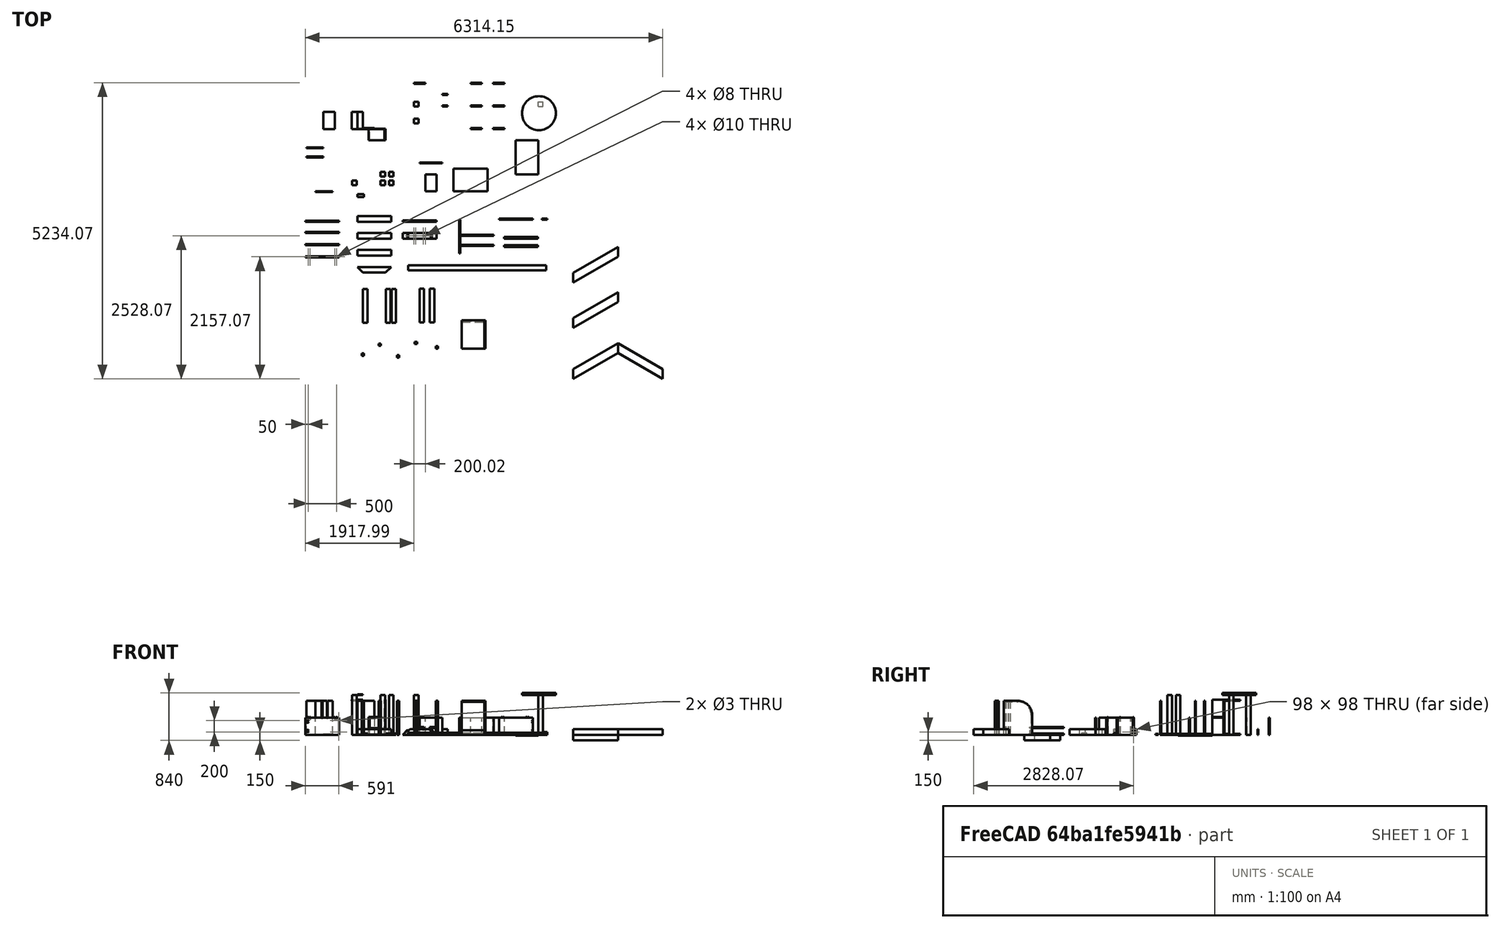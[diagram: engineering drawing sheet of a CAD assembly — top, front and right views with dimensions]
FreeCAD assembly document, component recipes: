
FREECAD ASSEMBLY — COMPONENT RECIPES ("Test001_features")

This assembly document has 28 components, labeled P0..P27 below (a component is one placed body or linked part). 21 of them carry a construction recipe — the FreeCAD feature program that regenerates the part from scratch, quoted from this document or its linked companion documents; the rest are supplied as boundary geometry only. No exploded tour is included for this assembly.
COMPONENT P0 — recipe-attached ("PDMirror Pad Body", modeled in this document).
Construction recipe (the document's own serialized feature program — sketch geometry with constraints, then the solid features built on it; lengths are millimeters unless a unit is written):

FEATURE [Sketcher::SketchObject] Sketch  label="Sketch001"
  ArcFitTolerance = 0
  AttachmentOffset = pos=(1300,-500,0) rot=(0,0,1;0rad)
  AttachmentSupport = -> [XY_Plane]
  ExternalTypes = [0]
  FullyConstrained = false
  MakeInternals = false
  MapMode = 5
  Placement = pos=(1300,-500,0) rot=(0,0,1;0rad)
  _ExternalGeoVersion = 0
  sketch-geometry (4):
    g0: LineSegment StartX=0 StartY=-90.3636 StartZ=0 EndX=200 EndY=-90.3636 EndZ=0
    g1: LineSegment StartX=200 StartY=-90.3636 StartZ=0 EndX=200 EndY=-108.364 EndZ=0
    g2: LineSegment StartX=200 StartY=-108.364 StartZ=0 EndX=0 EndY=-108.364 EndZ=0
    g3: LineSegment StartX=0 StartY=-108.364 StartZ=0 EndX=0 EndY=-90.3636 EndZ=0
  constraints (11):
    c: Coincident(g0,g1)
    c: Coincident(g1,g2)
    c: Coincident(g2,g3)
    c: Coincident(g3,g0)
    c: Horizontal(g0)
    c: Horizontal(g2)
    c: Vertical(g1)
    c: Vertical(g3)
    c: DistanceX(g0,g0) = 200
    c: DistanceY(g3,g3) = 18
    c: DistanceX(g-1,g0) = 200
FEATURE [PartDesign::Pad] Pad  label="PDMirror Pad"
  AllowMultiFace = false
  Direction = (0,0,1)
  Length = 300
  Length2 = 100
  Profile = -> Sketch
  SideType = 0
  Suppressed = false
  Type = 0
  Type2 = 0
FEATURE [PartDesign::Mirrored] Mirrored
  BaseFeature = -> Pad
  MirrorPlane = -> Sketch [V_Axis]
  Originals = -> [Pad]
  Suppressed = false
  TransformMode = 0
FEATURE [PartDesign::Body] Body  label="PDMirror Pad Body"
  AllowCompound = false
  Group = -> [Sketch,Pad,Mirrored]
  Origin = -> Origin
  Tip = -> Mirrored
COMPONENT P1 — recipe-attached ("Pad Single Body", modeled in this document).
Construction recipe (the document's own serialized feature program — sketch geometry with constraints, then the solid features built on it; lengths are millimeters unless a unit is written):

FEATURE [Sketcher::SketchObject] Sketch001  label="Sketch002"
  ArcFitTolerance = 0
  AttachmentOffset = pos=(1500,-1200,0) rot=(0,0,1;0rad)
  AttachmentSupport = -> [XY_Plane001]
  ExternalTypes = [0]
  FullyConstrained = true
  MakeInternals = false
  MapMode = 5
  Placement = pos=(1500,-1200,0) rot=(0,0,1;0rad)
  _ExternalGeoVersion = 0
  sketch-geometry (4):
    g0: LineSegment StartX=-300 StartY=400 StartZ=0 EndX=-100 EndY=400 EndZ=0
    g1: LineSegment StartX=-100 StartY=400 StartZ=0 EndX=-100 EndY=100 EndZ=0
    g2: LineSegment StartX=-100 StartY=100 StartZ=0 EndX=-300 EndY=100 EndZ=0
    g3: LineSegment StartX=-300 StartY=100 StartZ=0 EndX=-300 EndY=400 EndZ=0
  constraints (12):
    c: Coincident(g0,g1)
    c: Coincident(g1,g2)
    c: Coincident(g2,g3)
    c: Coincident(g3,g0)
    c: Horizontal(g0)
    c: Horizontal(g2)
    c: Vertical(g1)
    c: Vertical(g3)
    c: DistanceX(g0,g0) = 200
    c: DistanceY(g3,g3) = 300
    c: DistanceY(g-1,g0) = 400
    c: DistanceX(g1,g-1) = 100
FEATURE [PartDesign::Pad] Pad001  label="Pad Single"
  AllowMultiFace = false
  Direction = (0,0,1)
  Length = 18
  Length2 = 100
  Profile = -> Sketch001
  SideType = 0
  Suppressed = false
  Type = 0
  Type2 = 0
FEATURE [PartDesign::Body] Body001  label="Pad Single Body"
  AllowCompound = false
  Group = -> [Sketch001,Pad001]
  Origin = -> Origin001
  Tip = -> Pad001
COMPONENT P2 — recipe-attached ("PDMulti 4 Pad Body", modeled in this document).
Construction recipe (the document's own serialized feature program — sketch geometry with constraints, then the solid features built on it; lengths are millimeters unless a unit is written):

FEATURE [Sketcher::SketchObject] Sketch002  label="Sketch003"
  ArcFitTolerance = 0
  AttachmentOffset = pos=(2000,-900,0) rot=(0,0,1;0rad)
  AttachmentSupport = -> [XY_Plane002]
  ExternalTypes = [0]
  FullyConstrained = true
  MakeInternals = false
  MapMode = 5
  Placement = pos=(2000,-900,0) rot=(0,0,1;0rad)
  _ExternalGeoVersion = 0
  sketch-geometry (4):
    g0: LineSegment StartX=-300 StartY=200 StartZ=0 EndX=0 EndY=200 EndZ=0
    g1: LineSegment StartX=0 StartY=200 StartZ=0 EndX=0 EndY=0 EndZ=0
    g2: LineSegment StartX=0 StartY=0 StartZ=0 EndX=-300 EndY=0 EndZ=0
    g3: LineSegment StartX=-300 StartY=0 StartZ=0 EndX=-300 EndY=200 EndZ=0
  constraints (12):
    c: Coincident(g0,g1)
    c: Coincident(g1,g2)
    c: Coincident(g2,g3)
    c: Coincident(g3,g0)
    c: Horizontal(g0)
    c: Horizontal(g2)
    c: Vertical(g1)
    c: Vertical(g3)
    c: DistanceX(g0,g0) = 300
    c: DistanceY(g3,g3) = 200
    c: DistanceY(g1,g-1) = 0
    c: DistanceX(g1,g-1) = 0
FEATURE [PartDesign::Pad] Pad002  label="PDMulti 4 Pad"
  AllowMultiFace = false
  Direction = (0,0,1)
  Length = 18
  Length2 = 100
  Profile = -> Sketch002
  SideType = 0
  Suppressed = false
  Type = 0
  Type2 = 0
FEATURE [PartDesign::Mirrored] Mirrored001
  MirrorPlane = -> Sketch002 [V_Axis]
  Suppressed = false
  TransformMode = 0
FEATURE [PartDesign::Mirrored] Mirrored002
  MirrorPlane = -> Sketch002 [H_Axis]
  Suppressed = false
  TransformMode = 0
FEATURE [PartDesign::MultiTransform] MultiTransform
  BaseFeature = -> Pad002
  Originals = -> [Pad002]
  Suppressed = false
  TransformMode = 0
  Transformations = -> [Mirrored001,Mirrored002]
FEATURE [PartDesign::Body] Body002  label="PDMulti 4 Pad Body"
  AllowCompound = false
  Group = -> [Sketch002,Pad002,MultiTransform,Mirrored001,Mirrored002]
  Origin = -> Origin002
  Tip = -> MultiTransform
COMPONENT P3 — recipe-attached ("PDMulti 8 Pad Body", modeled in this document).
Construction recipe (the document's own serialized feature program — sketch geometry with constraints, then the solid features built on it; lengths are millimeters unless a unit is written):

FEATURE [Sketcher::SketchObject] Sketch003  label="Sketch004"
  ArcFitTolerance = 0
  AttachmentOffset = pos=(3000,-500,0) rot=(0,0,1;0rad)
  AttachmentSupport = -> [XY_Plane003]
  ExternalTypes = [0]
  FullyConstrained = true
  MakeInternals = false
  MapMode = 5
  Placement = pos=(3000,-500,0) rot=(0,0,1;0rad)
  _ExternalGeoVersion = 0
  sketch-geometry (4):
    g0: LineSegment StartX=-200 StartY=300 StartZ=0 EndX=0 EndY=300 EndZ=0
    g1: LineSegment StartX=0 StartY=300 StartZ=0 EndX=0 EndY=0 EndZ=0
    g2: LineSegment StartX=0 StartY=0 StartZ=0 EndX=-200 EndY=0 EndZ=0
    g3: LineSegment StartX=-200 StartY=0 StartZ=0 EndX=-200 EndY=300 EndZ=0
  constraints (11):
    c: Coincident(g0,g1)
    c: Coincident(g1,g2)
    c: Coincident(g2,g3)
    c: Coincident(g3,g0)
    c: Horizontal(g0)
    c: Horizontal(g2)
    c: Vertical(g1)
    c: Vertical(g3)
    c: Coincident(g1,g-1)
    c: DistanceX(g0,g0) = 200
    c: DistanceY(g3,g3) = 300
FEATURE [PartDesign::Pad] Pad003  label="PDMulti 8 Pad"
  AllowMultiFace = false
  Direction = (0,0,1)
  Length = 18
  Length2 = 100
  Profile = -> Sketch003
  SideType = 0
  Suppressed = false
  Type = 0
  Type2 = 0
FEATURE [PartDesign::Mirrored] Mirrored003
  MirrorPlane = -> Sketch003 [V_Axis]
  Suppressed = false
  TransformMode = 0
FEATURE [PartDesign::Mirrored] Mirrored004
  MirrorPlane = -> Sketch003 [H_Axis]
  Suppressed = false
  TransformMode = 0
FEATURE [PartDesign::Mirrored] Mirrored005
  MirrorPlane = -> XY_Plane003
  Suppressed = false
  TransformMode = 0
FEATURE [PartDesign::MultiTransform] MultiTransform001
  BaseFeature = -> Pad003
  Originals = -> [Pad003]
  Suppressed = false
  TransformMode = 0
  Transformations = -> [Mirrored003,Mirrored004,Mirrored005]
FEATURE [PartDesign::Body] Body003  label="PDMulti 8 Pad Body"
  AllowCompound = false
  Group = -> [Sketch003,Pad003,MultiTransform001,Mirrored003,Mirrored004,Mirrored005]
  Origin = -> Origin003
  Tip = -> MultiTransform001
COMPONENT P4 — recipe-attached ("Array Pad Body", modeled in this document).
Construction recipe (the document's own serialized feature program — sketch geometry with constraints, then the solid features built on it; lengths are millimeters unless a unit is written):

FEATURE [Sketcher::SketchObject] Sketch004  label="Sketch005"
  ArcFitTolerance = 0
  AttachmentOffset = pos=(500,-1000,0) rot=(0,0,1;0rad)
  AttachmentSupport = -> [XY_Plane004]
  ExternalTypes = [0]
  FullyConstrained = true
  MakeInternals = false
  MapMode = 5
  Placement = pos=(500,-1000,0) rot=(0,0,1;0rad)
  _ExternalGeoVersion = 0
  sketch-geometry (4):
    g0: LineSegment StartX=-90 StartY=90 StartZ=0 EndX=-10 EndY=90 EndZ=0
    g1: LineSegment StartX=-10 StartY=90 StartZ=0 EndX=-10 EndY=10 EndZ=0
    g2: LineSegment StartX=-10 StartY=10 StartZ=0 EndX=-90 EndY=10 EndZ=0
    g3: LineSegment StartX=-90 StartY=10 StartZ=0 EndX=-90 EndY=90 EndZ=0
  constraints (12):
    c: Coincident(g0,g1)
    c: Coincident(g1,g2)
    c: Coincident(g2,g3)
    c: Coincident(g3,g0)
    c: Horizontal(g0)
    c: Horizontal(g2)
    c: Vertical(g1)
    c: Vertical(g3)
    c: DistanceY(g-1,g1) = 10
    c: DistanceX(g1,g-1) = 10
    c: DistanceX(g0,g0) = 80
    c: DistanceY(g3,g3) = 80
FEATURE [PartDesign::Pad] Pad004  label="Array Pad"
  AllowMultiFace = false
  Direction = (0,0,1)
  Length = 700
  Length2 = 100
  Profile = -> Sketch004
  SideType = 0
  Suppressed = false
  Type = 0
  Type2 = 0
FEATURE [PartDesign::Body] Body004  label="Array Pad Body"
  AllowCompound = false
  Group = -> [Sketch004,Pad004]
  Origin = -> Origin004
  Tip = -> Pad004
COMPONENT P5 — recipe-attached ("Array Polar Pad Body", modeled in this document).
Construction recipe (the document's own serialized feature program — sketch geometry with constraints, then the solid features built on it; lengths are millimeters unless a unit is written):

FEATURE [Sketcher::SketchObject] Sketch005  label="Sketch006"
  ArcFitTolerance = 0
  AttachmentOffset = pos=(0,-1000,0) rot=(0,0,1;0rad)
  AttachmentSupport = -> [XY_Plane005]
  ExternalTypes = [0]
  FullyConstrained = true
  MakeInternals = false
  MapMode = 5
  Placement = pos=(0,-1000,0) rot=(0,0,1;0rad)
  _ExternalGeoVersion = 0
  sketch-geometry (4):
    g0: LineSegment StartX=-90 StartY=90 StartZ=0 EndX=-10 EndY=90 EndZ=0
    g1: LineSegment StartX=-10 StartY=90 StartZ=0 EndX=-10 EndY=10 EndZ=0
    g2: LineSegment StartX=-10 StartY=10 StartZ=0 EndX=-90 EndY=10 EndZ=0
    g3: LineSegment StartX=-90 StartY=10 StartZ=0 EndX=-90 EndY=90 EndZ=0
  constraints (12):
    c: Coincident(g0,g1)
    c: Coincident(g1,g2)
    c: Coincident(g2,g3)
    c: Coincident(g3,g0)
    c: Horizontal(g0)
    c: Horizontal(g2)
    c: Vertical(g1)
    c: Vertical(g3)
    c: DistanceY(g-1,g1) = 10
    c: DistanceX(g1,g-1) = 10
    c: DistanceX(g0,g0) = 80
    c: DistanceY(g3,g3) = 80
FEATURE [PartDesign::Pad] Pad005  label="Array Polar Pad"
  AllowMultiFace = false
  Direction = (0,0,1)
  Length = 700
  Length2 = 100
  Profile = -> Sketch005
  SideType = 0
  Suppressed = false
  Type = 0
  Type2 = 0
FEATURE [PartDesign::Body] Body005  label="Array Polar Pad Body"
  AllowCompound = false
  Group = -> [Sketch005,Pad005]
  Origin = -> Origin005
  Tip = -> Pad005
COMPONENT P6 — recipe-attached ("Table Top Parent Body", modeled in this document).
Construction recipe (the document's own serialized feature program — sketch geometry with constraints, then the solid features built on it; lengths are millimeters unless a unit is written):

FEATURE [Sketcher::SketchObject] Sketch006  label="Sketch007"
  ArcFitTolerance = 0
  AttachmentOffset = pos=(0,0,700) rot=(0,0,1;0rad)
  AttachmentSupport = -> [XY_Plane006]
  ExternalTypes = [0]
  FullyConstrained = false
  MakeInternals = false
  MapMode = 5
  Placement = pos=(0,0,700) rot=(0,0,1;0rad)
  _ExternalGeoVersion = 0
  sketch-geometry (1):
    g0: Circle CenterX=3208.45 CenterY=279.77 CenterZ=0 NormalX=0 NormalY=0 NormalZ=1 AngleXU=0 Radius=300
  constraints (1):
    c: Radius(g0) = 300  'This is my round table top radius'
FEATURE [PartDesign::Pad] Pad006  label="Table Top"
  Direction = (0,0,1)
  Length = 40
  Length2 = 100
  Profile = -> Sketch006
  SideType = 0
  Suppressed = false
  Type = 0
  Type2 = 0
FEATURE [PartDesign::Body] Body006  label="Table Top Parent Body"
  AllowCompound = false
  Group = -> [Sketch006,Pad006]
  Origin = -> Origin006
  Tip = -> Pad006
COMPONENT P7 — recipe-attached ("Screw, Body", modeled in this document).
Construction recipe (the document's own serialized feature program — sketch geometry with constraints, then the solid features built on it; lengths are millimeters unless a unit is written):

FEATURE [Sketcher::SketchObject] Sketch007  label="Core, Pattern"
  ArcFitTolerance = 0
  AttachmentSupport = -> [XZ_Plane007]
  ExternalTypes = [0]
  FullyConstrained = true
  MakeInternals = false
  MapMode = 5
  Placement = pos=(0,0,0) rot=(1,0,0;1.5708rad)
  _ExternalGeoVersion = 0
  expr: Constraints[10] = Spreadsheet.corer
  expr: Constraints[11] = 2 * Spreadsheet.tjump
  expr: Constraints[12] = Spreadsheet.sheight
  expr: Constraints[13] = Spreadsheet.hheight1
  expr: Constraints[14] = Spreadsheet.hheight2
  expr: Constraints[15] = Spreadsheet.hr
  expr: Constraints[16] = Spreadsheet.hheight1
  sketch-geometry (6):
    g0: LineSegment StartX=0 StartY=0 StartZ=0 EndX=1.5 EndY=3.8 EndZ=0
    g1: LineSegment StartX=1.5 StartY=3.8 StartZ=0 EndX=1.5 EndY=37 EndZ=0
    g2: LineSegment StartX=1.5 StartY=37 StartZ=0 EndX=2 EndY=37.5 EndZ=0
    g3: LineSegment StartX=2 StartY=37.5 StartZ=0 EndX=3.87 EndY=40 EndZ=0
    g4: LineSegment StartX=3.87 StartY=40 StartZ=0 EndX=0 EndY=40 EndZ=0
    g5: LineSegment StartX=0 StartY=40 StartZ=0 EndX=0 EndY=0 EndZ=0
  constraints (17):
    c: Coincident(g-1,g0)
    c: Coincident(g0,g1)
    c: Vertical(g1)
    c: Coincident(g1,g2)
    c: Coincident(g2,g3)
    c: Coincident(g3,g4)
    c: PointOnObject(g4,g-2)
    c: Horizontal(g4)
    c: Coincident(g4,g5)
    c: Coincident(g5,g0)
    c: DistanceX(g0,g0) = 1.5
    c: DistanceY(g0,g0) = 3.8
    c: DistanceY(g5,g5) = 40
    c: DistanceY(g1,g2) = 0.5
    c: DistanceY(g2,g3) = 2.5
    c: DistanceX(g4,g3) = 3.87
    c: DistanceX(g1,g2) = 0.5
FEATURE [PartDesign::Revolution] Revolution  label="Core"
  Angle = 360
  Angle2 = 60
  Axis = (0,2e-16,1)
  Base = (0,0,0)
  FuseOrder = 0
  Placement = pos=(0,0,0) rot=(1,0,0;1.5708rad)
  Profile = -> Sketch007
  ReferenceAxis = -> Sketch007 [V_Axis]
  Reversed = true
  Suppressed = false
  Type = 0
FEATURE [Sketcher::SketchObject] Sketch008  label="Thread, Pattern"
  ArcFitTolerance = 0
  AttachmentSupport = -> [XZ_Plane007]
  ExternalTypes = [0]
  FullyConstrained = true
  MakeInternals = false
  MapMode = 5
  Placement = pos=(0,0,0) rot=(1,0,0;1.5708rad)
  _ExternalGeoVersion = 0
  expr: Constraints[2] = Spreadsheet.spikesize
  expr: Constraints[3] = Spreadsheet.corer
  sketch-geometry (3):
    g0: LineSegment StartX=1.5 StartY=3.675 StartZ=0 EndX=2 EndY=3.8 EndZ=0
    g1: LineSegment StartX=2 StartY=3.8 StartZ=0 EndX=1.5 EndY=3.925 EndZ=0
    g2: LineSegment StartX=1.5 StartY=3.925 StartZ=0 EndX=1.5 EndY=3.675 EndZ=0
  constraints (9):
    c: Coincident(g0,g1)
    c: Equal(g0,g1)
    c: DistanceY(g-1,g0) = 3.8
    c: DistanceX(g-1,g0) = 1.5
    c: DistanceX(g0,g0) = 0.5
    c: DistanceY(g0,g1) = 0.25
    c: Vertical(g1,g0)
    c: Coincident(g2,g1)
    c: Coincident(g2,g0)
FEATURE [PartDesign::AdditiveHelix] AdditiveHelix  label="Thread, Core"
  Angle = 0
  Axis = (0,2e-16,1)
  Base = (0,0,0)
  BaseFeature = -> Revolution
  Growth = 0
  HasBeenEdited = true
  Height = 20.4
  LeftHanded = false
  Mode = 0
  Outside = false
  Pitch = 1.9
  Placement = pos=(0,0,0) rot=(1,0,0;1.5708rad)
  Profile = -> Sketch008
  ReferenceAxis = -> Sketch008 [V_Axis]
  Suppressed = false
  Tolerance = 0.1
  Turns = 10.7368
  expr: Height = Spreadsheet.theight - Spreadsheet.spikesize
  expr: Pitch = Spreadsheet.tjump
FEATURE [PartDesign::AdditiveHelix] AdditiveHelix001  label="Thread, Spike"
  Angle = -30
  Axis = (0,2e-16,1)
  Base = (0,0,0)
  BaseFeature = -> AdditiveHelix
  Growth = -1.09697
  HasBeenEdited = true
  Height = 2.53333
  LeftHanded = false
  Mode = 0
  Outside = false
  Pitch = 1.9
  Placement = pos=(0,0,0) rot=(1,0,0;1.5708rad)
  Profile = -> Sketch008
  ReferenceAxis = -> Sketch008 [V_Axis]
  Reversed = true
  Suppressed = false
  Tolerance = 0.1
  Turns = 1.33333
  expr: Height = 2 * Spreadsheet.spikesize / 3
  expr: Pitch = Spreadsheet.tjump
FEATURE [Sketcher::SketchObject] Sketch009  label="Bit, Pattern 1"
  ArcFitTolerance = 0
  AttachmentSupport = -> [YZ_Plane007]
  ExternalTypes = [0]
  FullyConstrained = true
  MakeInternals = false
  MapMode = 5
  Placement = pos=(0,0,0) rot=(0.57735,0.57735,0.57735;2.0944rad)
  _ExternalGeoVersion = 0
  expr: Constraints[16] = Spreadsheet.hheight2 / 4
  expr: Constraints[6] = Spreadsheet.coredia
  expr: Constraints[7] = Spreadsheet.sheight
  expr: Constraints[8] = Spreadsheet.bitsize
  expr: Constraints[9] = Spreadsheet.hheight2 / 2
  sketch-geometry (6):
    g0: LineSegment StartX=-2.13 StartY=40 StartZ=0 EndX=2.13 EndY=40 EndZ=0
    g1: LineSegment StartX=2.13 StartY=40 StartZ=0 EndX=1.5 EndY=38.75 EndZ=0
    g2: LineSegment StartX=1.5 StartY=38.75 StartZ=0 EndX=0.875 EndY=38.75 EndZ=0
    g3: LineSegment StartX=-1.5 StartY=38.75 StartZ=0 EndX=-2.13 EndY=40 EndZ=0
    g4: ArcOfCircle CenterX=0 CenterY=40 CenterZ=0 NormalX=0 NormalY=0 NormalZ=1 AngleXU=0 Radius=1.52582 StartAngle=4.10166 EndAngle=5.32311
    g5: LineSegment StartX=-0.875 StartY=38.75 StartZ=0 EndX=-1.5 EndY=38.75 EndZ=0
  constraints (17):
    c: Coincident(g0,g1)
    c: Coincident(g1,g2)
    c: Coincident(g5,g3)
    c: Coincident(g3,g0)
    c: Symmetric(g1,g5,g-2)
    c: Symmetric(g0,g0,g-2)
    c: DistanceX(g5,g2) = 3
    c: DistanceY(g-1,g0) = 40
    c: DistanceX(g0,g0) = 4.26
    c: DistanceY(g1,g0) = 1.25
    c: Horizontal(g4,g0)
    c: PointOnObject(g4,g-2)
    c: Coincident(g2,g4)
    c: Coincident(g5,g4)
    c: Horizontal(g3,g4)
    c: Horizontal(g4,g2)
    c: DistanceX(g2,g1) = 0.625
FEATURE [PartDesign::Pocket] Pocket  label="Bit, Pocket 1"
  BaseFeature = -> AdditiveHelix001
  Direction = (-1,0,0)
  Length = 1
  Length2 = 5
  Placement = pos=(0,0,0) rot=(1,0,0;1.5708rad)
  Profile = -> Sketch009
  ReferenceAxis = -> Sketch009 [N_Axis]
  SideType = 2
  Suppressed = false
  Type = 0
  Type2 = 0
FEATURE [Sketcher::SketchObject] Sketch010  label="Bit, Line, Pattern 1"
  ArcFitTolerance = 0
  AttachmentOffset = pos=(0,0,0) rot=(0,1,0;0.785398rad)
  AttachmentSupport = -> [YZ_Plane007]
  ExternalTypes = [0]
  FullyConstrained = true
  MakeInternals = false
  MapMode = 5
  Placement = pos=(0,0,0) rot=(0.281085,0.678598,0.678598;2.59356rad)
  _ExternalGeoVersion = 0
  expr: Constraints[10] = Spreadsheet.sheight
  expr: Constraints[6] = Spreadsheet.bitsize
  sketch-geometry (4):
    g0: LineSegment StartX=2.13 StartY=40 StartZ=0 EndX=2.13 EndY=39.9 EndZ=0
    g1: LineSegment StartX=2.13 StartY=39.9 StartZ=0 EndX=-2.13 EndY=39.9 EndZ=0
    g2: LineSegment StartX=-2.13 StartY=39.9 StartZ=0 EndX=-2.13 EndY=40 EndZ=0
    g3: LineSegment StartX=-2.13 StartY=40 StartZ=0 EndX=2.13 EndY=40 EndZ=0
  constraints (11):
    c: Coincident(g0,g1)
    c: Coincident(g1,g2)
    c: Coincident(g3,g2)
    c: Coincident(g3,g0)
    c: Equal(g1,g3)
    c: Equal(g0,g2)
    c: DistanceX(g3,g3) = 4.26
    c: Vertical(g2)
    c: Symmetric(g1,g0,g-2)
    c: DistanceY(g0,g0) = 0.1
    c: DistanceY(g-1,g0) = 40
FEATURE [PartDesign::Pocket] Pocket001  label="Bit, Lines 1"
  BaseFeature = -> Pocket
  Direction = (-0.707107,-0.707107,0)
  Length = 0.1
  Length2 = 5
  Placement = pos=(0,0,0) rot=(1,0,0;1.5708rad)
  Profile = -> Sketch010
  ReferenceAxis = -> Sketch010 [N_Axis]
  SideType = 2
  Suppressed = false
  Type = 0
  Type2 = 0
FEATURE [PartDesign::PolarPattern] PolarPattern  label="Bit, PolarPattern"
  Angle = 90
  Axis = -> Sketch010 [V_Axis]
  BaseFeature = -> Pocket001
  Mode = 0
  Occurrences = 2
  Offset = 120
  Originals = -> [Pocket001,Pocket]
  Placement = pos=(0,0,0) rot=(1,0,0;1.5708rad)
  SpacingPattern = [0]
  Spacings = [-1]
  Suppressed = false
  TransformMode = 0
FEATURE [Sketcher::SketchObject] Sketch011  label="Thread, Top, Pattern"
  ArcFitTolerance = 0
  AttachmentSupport = -> [XZ_Plane007]
  ExternalTypes = [0]
  FullyConstrained = true
  MakeInternals = false
  MapMode = 5
  Placement = pos=(0,0,0) rot=(1,0,0;1.5708rad)
  _ExternalGeoVersion = 0
  expr: Constraints[2] = Spreadsheet.tjump
  expr: Constraints[4] = Spreadsheet.corer
  expr: Constraints[5] = Spreadsheet.theight
  sketch-geometry (4):
    g0: LineSegment StartX=1.5 StartY=26.1 StartZ=0 EndX=1.5 EndY=24.2 EndZ=0
    g1: LineSegment StartX=1.5 StartY=24.2 StartZ=0 EndX=2.5 EndY=24.2 EndZ=0
    g2: LineSegment StartX=1.5 StartY=26.1 StartZ=0 EndX=2.5 EndY=26.1 EndZ=0
    g3: LineSegment StartX=2.5 StartY=26.1 StartZ=0 EndX=2.5 EndY=24.2 EndZ=0
  constraints (12):
    c: Vertical(g0)
    c: Coincident(g0,g1)
    c: DistanceY(g0,g0) = 1.9
    c: DistanceX(g0,g1) = 1
    c: DistanceX(g-1,g0) = 1.5
    c: DistanceY(g-1,g1) = 24.2
    c: Coincident(g0,g2)
    c: Coincident(g2,g3)
    c: Coincident(g3,g1)
    c: Horizontal(g2)
    c: Vertical(g3)
    c: Horizontal(g1)
FEATURE [PartDesign::SubtractiveHelix] SubtractiveHelix  label="Thread, Top"
  Angle = 15
  Axis = (0,2e-16,1)
  Base = (0,0,0)
  BaseFeature = -> PolarPattern
  Growth = 0.509103
  HasBeenEdited = true
  Height = 1.9
  LeftHanded = false
  Mode = 0
  Outside = false
  Pitch = 1.9
  Placement = pos=(0,0,0) rot=(1,0,0;1.5708rad)
  Profile = -> Sketch011
  ReferenceAxis = -> Sketch011 [V_Axis]
  Reversed = true
  Suppressed = false
  Tolerance = 0.1
  Turns = 1
  expr: Height = Spreadsheet.tjump
  expr: Pitch = Spreadsheet.tjump
FEATURE [PartDesign::Body] Body007  label="Screw, Body"
  AllowCompound = false
  Group = -> [Sketch007,Revolution,Sketch008,AdditiveHelix,AdditiveHelix001,Sketch009,Pocket,Sketch010,Pocket001,PolarPattern,Sketch011,SubtractiveHelix]
  Origin = -> Origin007
  Tip = -> SubtractiveHelix
COMPONENT P8 — geometry summary ("Link"; no construction recipe available for this part):
  bounding box: 600.0 x 300.0 x 180.0 mm
  tessellated surface: 24 triangles
  volume: 6480000 mm^3 (20% of its bounding box)
  symmetry: 2-fold rotationally symmetric about the x axis; 2-fold rotationally symmetric about the y axis; 2-fold rotationally symmetric about the z axis; mirror-symmetric across its x mid-plane, y mid-plane, z mid-plane
COMPONENT P9 — geometry summary ("Link, Cut"; no construction recipe available for this part):
  bounding box: 600.0 x 300.0 x 18.0 mm
  tessellated surface: 44 triangles
  volume: 3037824 mm^3 (94% of its bounding box)
  symmetry: mirror-symmetric across its y mid-plane
COMPONENT P10 — geometry summary ("Link, nested 1 link "; no construction recipe available for this part):
  bounding box: 600.0 x 180.0 x 20.0 mm
  tessellated surface: 24 triangles
  volume: 1920000 mm^3 (89% of its bounding box)
  symmetry: 2-fold rotationally symmetric about the x axis; 2-fold rotationally symmetric about the y axis; 2-fold rotationally symmetric about the z axis; mirror-symmetric across its x mid-plane, y mid-plane, z mid-plane
COMPONENT P11 — geometry summary ("Link, nested 2 link"; no construction recipe available for this part):
  bounding box: 600.0 x 180.0 x 20.0 mm
  tessellated surface: 24 triangles
  volume: 1920000 mm^3 (89% of its bounding box)
  symmetry: 2-fold rotationally symmetric about the x axis; 2-fold rotationally symmetric about the y axis; 2-fold rotationally symmetric about the z axis; mirror-symmetric across its x mid-plane, y mid-plane, z mid-plane
COMPONENT P12 — recipe-attached ("Link, panelZX002 ", modeled in this document).
Construction recipe (the document's own serialized feature program — sketch geometry with constraints, then the solid features built on it; lengths are millimeters unless a unit is written):

FEATURE [Sketcher::SketchObject] Sketch035  label="Pattern, panel2pad001"
  ArcFitTolerance = 0
  AttachmentSupport = -> [XZ_Plane025]
  ExternalTypes = [0]
  FullyConstrained = true
  MakeInternals = false
  MapMode = 5
  Placement = pos=(0,0,0) rot=(1,0,0;1.5708rad)
  _ExternalGeoVersion = 0
  sketch-geometry (4):
    g0: LineSegment StartX=0 StartY=600 StartZ=0 EndX=300 EndY=600 EndZ=0
    g1: LineSegment StartX=300 StartY=600 StartZ=0 EndX=300 EndY=0 EndZ=0
    g2: LineSegment StartX=300 StartY=0 StartZ=0 EndX=0 EndY=0 EndZ=0
    g3: LineSegment StartX=0 StartY=0 StartZ=0 EndX=0 EndY=600 EndZ=0
  constraints (11):
    c: Coincident(g0,g1)
    c: Coincident(g1,g2)
    c: Coincident(g2,g3)
    c: Coincident(g3,g0)
    c: Horizontal(g0)
    c: Horizontal(g2)
    c: Vertical(g1)
    c: Vertical(g3)
    c: Coincident(g2,g-1)
    c: DistanceX(g0,g0) = 300  'SizeX'
    c: DistanceY(g3,g3) = 600  'SizeY'
FEATURE [PartDesign::Pad] Pad015  label="panel2pad"
  Direction = (0,-1,2e-16)
  Length = 18
  Length2 = 10
  Placement = pos=(0,0,0) rot=(1,0,0;1.5708rad)
  Profile = -> Sketch035
  Reversed = true
  SideType = 0
  Suppressed = false
  Type = 0
  Type2 = 0
FEATURE [Sketcher::SketchObject] routerPattern002
  ArcFitTolerance = 0
  ExternalTypes = [0]
  FullyConstrained = true
  MakeInternals = false
  Placement = pos=(150,1.332e-13,600) rot=(0,1,0;1.5708rad)
  _ExternalGeoVersion = 0
  sketch-geometry (4):
    g0: ArcOfCircle CenterX=18 CenterY=-18 CenterZ=0 NormalX=0 NormalY=0 NormalZ=1 AngleXU=0 Radius=18 StartAngle=1.5708 EndAngle=3.14159
    g1: ArcOfCircle CenterX=-18 CenterY=18 CenterZ=0 NormalX=0 NormalY=0 NormalZ=1 AngleXU=0 Radius=18 StartAngle=4.71239 EndAngle=6.28319
    g2: ArcOfCircle CenterX=18 CenterY=18 CenterZ=0 NormalX=0 NormalY=0 NormalZ=1 AngleXU=0 Radius=18 StartAngle=3.14159 EndAngle=4.71239
    g3: ArcOfCircle CenterX=-18 CenterY=-18 CenterZ=0 NormalX=0 NormalY=0 NormalZ=1 AngleXU=0 Radius=18 StartAngle=6.28318 EndAngle=7.85398
  constraints (16):
    c: Equal(g3,g1)
    c: Equal(g1,g2)
    c: Equal(g2,g0)
    c: Vertical(g0,g2)
    c: Horizontal(g3,g0)
    c: Vertical(g1,g3)
    c: Horizontal(g1,g2)
    c: Coincident(g1,g2)
    c: Coincident(g0,g2)
    c: Coincident(g3,g0)
    c: Coincident(g3,g1)
    c: PointOnObject(g1,g-1)
    c: PointOnObject(g1,g-2)
    c: DistanceY(g0,g-1) = 18
    c: Vertical(g0,g0)
    c: Horizontal(g1,g1)
FEATURE [PartDesign::Pocket] router002  label="RoundOver "
  BaseFeature = -> Pad015
  Direction = (-1,0,-2e-16)
  Length = 5
  Length2 = 5
  Placement = pos=(0,0,0) rot=(1,0,0;1.5708rad)
  Profile = -> routerPattern002
  SideType = 2
  Suppressed = false
  Type = 1
  Type2 = 0
FEATURE [Sketcher::SketchObject] routerPattern003
  ArcFitTolerance = 0
  ExternalTypes = [0]
  FullyConstrained = true
  MakeInternals = false
  Placement = pos=(300,6.7e-14,300) rot=(0,0,1;0rad)
  _ExternalGeoVersion = 0
  sketch-geometry (4):
    g0: ArcOfCircle CenterX=18 CenterY=-18 CenterZ=0 NormalX=0 NormalY=0 NormalZ=1 AngleXU=0 Radius=18 StartAngle=1.5708 EndAngle=3.14159
    g1: ArcOfCircle CenterX=-18 CenterY=18 CenterZ=0 NormalX=0 NormalY=0 NormalZ=1 AngleXU=0 Radius=18 StartAngle=4.71239 EndAngle=6.28319
    g2: ArcOfCircle CenterX=18 CenterY=18 CenterZ=0 NormalX=0 NormalY=0 NormalZ=1 AngleXU=0 Radius=18 StartAngle=3.14159 EndAngle=4.71239
    g3: ArcOfCircle CenterX=-18 CenterY=-18 CenterZ=0 NormalX=0 NormalY=0 NormalZ=1 AngleXU=0 Radius=18 StartAngle=6.28318 EndAngle=7.85398
  constraints (16):
    c: Equal(g3,g1)
    c: Equal(g1,g2)
    c: Equal(g2,g0)
    c: Vertical(g0,g2)
    c: Horizontal(g3,g0)
    c: Vertical(g1,g3)
    c: Horizontal(g1,g2)
    c: Coincident(g1,g2)
    c: Coincident(g0,g2)
    c: Coincident(g3,g0)
    c: Coincident(g3,g1)
    c: PointOnObject(g1,g-1)
    c: PointOnObject(g1,g-2)
    c: DistanceY(g0,g-1) = 18
    c: Vertical(g0,g0)
    c: Horizontal(g1,g1)
FEATURE [PartDesign::Pocket] router003  label="RoundOver 001"
  BaseFeature = -> router002
  Direction = (0,0,-1)
  Length = 5
  Length2 = 5
  Placement = pos=(0,0,0) rot=(1,0,0;1.5708rad)
  Profile = -> routerPattern003
  SideType = 2
  Suppressed = false
  Type = 1
  Type2 = 0
FEATURE [Sketcher::SketchObject] routerPattern004
  ArcFitTolerance = 0
  ExternalTypes = [0]
  FullyConstrained = true
  MakeInternals = false
  Placement = pos=(150,0,0) rot=(0,1,0;1.5708rad)
  _ExternalGeoVersion = 0
  sketch-geometry (4):
    g0: ArcOfCircle CenterX=18 CenterY=-18 CenterZ=0 NormalX=0 NormalY=0 NormalZ=1 AngleXU=0 Radius=18 StartAngle=1.5708 EndAngle=3.14159
    g1: ArcOfCircle CenterX=-18 CenterY=18 CenterZ=0 NormalX=0 NormalY=0 NormalZ=1 AngleXU=0 Radius=18 StartAngle=4.71239 EndAngle=6.28319
    g2: ArcOfCircle CenterX=18 CenterY=18 CenterZ=0 NormalX=0 NormalY=0 NormalZ=1 AngleXU=0 Radius=18 StartAngle=3.14159 EndAngle=4.71239
    g3: ArcOfCircle CenterX=-18 CenterY=-18 CenterZ=0 NormalX=0 NormalY=0 NormalZ=1 AngleXU=0 Radius=18 StartAngle=1.97117e-06 EndAngle=1.5708
  constraints (16):
    c: Equal(g3,g1)
    c: Equal(g1,g2)
    c: Equal(g2,g0)
    c: Vertical(g0,g2)
    c: Horizontal(g3,g0)
    c: Vertical(g1,g3)
    c: Horizontal(g1,g2)
    c: Coincident(g1,g2)
    c: Coincident(g0,g2)
    c: Coincident(g3,g0)
    c: Coincident(g3,g1)
    c: PointOnObject(g1,g-1)
    c: PointOnObject(g1,g-2)
    c: DistanceY(g0,g-1) = 18
    c: Vertical(g0,g0)
    c: Horizontal(g1,g1)
FEATURE [PartDesign::Pocket] router004  label="RoundOver 002"
  BaseFeature = -> router003
  Direction = (-1,0,-2e-16)
  Length = 5
  Length2 = 5
  Placement = pos=(0,0,0) rot=(1,0,0;1.5708rad)
  Profile = -> routerPattern004
  SideType = 2
  Suppressed = false
  Type = 1
  Type2 = 0
FEATURE [Sketcher::SketchObject] routerPattern005
  ArcFitTolerance = 0
  ExternalTypes = [0]
  FullyConstrained = true
  MakeInternals = false
  Placement = pos=(0,6.7e-14,300) rot=(0,0,1;0rad)
  _ExternalGeoVersion = 0
  sketch-geometry (4):
    g0: ArcOfCircle CenterX=18 CenterY=-18 CenterZ=0 NormalX=0 NormalY=0 NormalZ=1 AngleXU=0 Radius=18 StartAngle=1.5708 EndAngle=3.14159
    g1: ArcOfCircle CenterX=-18 CenterY=18 CenterZ=0 NormalX=0 NormalY=0 NormalZ=1 AngleXU=0 Radius=18 StartAngle=4.71239 EndAngle=6.28319
    g2: ArcOfCircle CenterX=18 CenterY=18 CenterZ=0 NormalX=0 NormalY=0 NormalZ=1 AngleXU=0 Radius=18 StartAngle=3.14159 EndAngle=4.71239
    g3: ArcOfCircle CenterX=-18 CenterY=-18 CenterZ=0 NormalX=0 NormalY=0 NormalZ=1 AngleXU=0 Radius=18 StartAngle=6.28318 EndAngle=7.85398
  constraints (16):
    c: Equal(g3,g1)
    c: Equal(g1,g2)
    c: Equal(g2,g0)
    c: Vertical(g0,g2)
    c: Horizontal(g3,g0)
    c: Vertical(g1,g3)
    c: Horizontal(g1,g2)
    c: Coincident(g1,g2)
    c: Coincident(g0,g2)
    c: Coincident(g3,g0)
    c: Coincident(g3,g1)
    c: PointOnObject(g1,g-1)
    c: PointOnObject(g1,g-2)
    c: DistanceY(g0,g-1) = 18
    c: Vertical(g0,g0)
    c: Horizontal(g1,g1)
FEATURE [PartDesign::Pocket] router005  label="RoundOver 003"
  BaseFeature = -> router004
  Direction = (0,0,-1)
  Length = 5
  Length2 = 5
  Placement = pos=(0,0,0) rot=(1,0,0;1.5708rad)
  Profile = -> routerPattern005
  SideType = 2
  Suppressed = false
  Type = 1
  Type2 = 0
FEATURE [PartDesign::Body] Body016  label="Body, panel2pad001"
  AllowCompound = false
  Group = -> [Sketch035,Pad015,routerPattern002,router002,routerPattern003,router003,routerPattern004,router004,routerPattern005,router005]
  Origin = -> Origin025
  Tip = -> router005
COMPONENT P13 — same part as P12; its construction recipe is shown at P12.
COMPONENT P14 — geometry summary ("Link, Screw 4 x 40 mm "; no construction recipe available for this part):
  bounding box: 40.0 x 7.7 x 7.4 mm
  tessellated surface: 486 triangles
  volume: 317 mm^3 (14% of its bounding box)
COMPONENT P15 — geometry summary ("Link, Screw 4 x 40 mm 001"; no construction recipe available for this part):
  bounding box: 40.0 x 7.7 x 7.4 mm
  tessellated surface: 486 triangles
  volume: 317 mm^3 (14% of its bounding box)
COMPONENT P16 — recipe-attached ("Part, Construction", modeled in this document).
Construction recipe (the document's own serialized feature program — sketch geometry with constraints, then the solid features built on it; lengths are millimeters unless a unit is written):

FEATURE [Sketcher::SketchObject] Sketch012  label="Pattern, Construction"
  ArcFitTolerance = 0
  AttachmentOffset = pos=(0,-1638,0) rot=(0,0,1;0rad)
  AttachmentSupport = -> [XY_Plane009]
  ExternalTypes = [0]
  FullyConstrained = true
  MakeInternals = false
  MapMode = 5
  Placement = pos=(0,-1638,0) rot=(0,0,1;0rad)
  _ExternalGeoVersion = 0
  sketch-geometry (4):
    g0: LineSegment StartX=0 StartY=100 StartZ=0 EndX=600 EndY=100 EndZ=0
    g1: LineSegment StartX=600 StartY=100 StartZ=0 EndX=600 EndY=0 EndZ=0
    g2: LineSegment StartX=600 StartY=0 StartZ=0 EndX=0 EndY=0 EndZ=0
    g3: LineSegment StartX=0 StartY=0 StartZ=0 EndX=0 EndY=100 EndZ=0
  constraints (11):
    c: Coincident(g0,g1)
    c: Coincident(g1,g2)
    c: Coincident(g2,g3)
    c: Coincident(g3,g0)
    c: Horizontal(g0)
    c: Horizontal(g2)
    c: Vertical(g1)
    c: Vertical(g3)
    c: Coincident(g2,g-1)
    c: DistanceX(g0,g0) = 600  'SizeX'
    c: DistanceY(g3,g3) = 100  'SizeY'
FEATURE [PartDesign::Pad] Pad007  label="Profile Simple"
  Direction = (0,0,1)
  Length = 100
  Length2 = 10
  Profile = -> Sketch012
  SideType = 0
  Suppressed = false
  Type = 0
  Type2 = 0
FEATURE [PartDesign::Thickness] Profile
  Base = -> Pad007 [Face2,Face4]
  BaseFeature = -> Pad007
  Intersection = false
  Join = 0
  Mode = 0
  Reversed = true
  SupportTransform = false
  Suppressed = false
  Value = 1
FEATURE [PartDesign::Body] Body008  label="Body, Construction"
  AllowCompound = false
  Group = -> [Sketch012,Pad007,Profile]
  Origin = -> Origin009
  Tip = -> Profile
COMPONENT P17 — recipe-attached ("Part, Construction001", modeled in this document).
Construction recipe (the document's own serialized feature program — sketch geometry with constraints, then the solid features built on it; lengths are millimeters unless a unit is written):

FEATURE [Sketcher::SketchObject] Sketch013  label="Pattern, Construction001"
  ArcFitTolerance = 0
  AttachmentOffset = pos=(0,-1938,0) rot=(0,0,1;0rad)
  AttachmentSupport = -> [XY_Plane011]
  ExternalTypes = [0]
  FullyConstrained = true
  MakeInternals = false
  MapMode = 5
  Placement = pos=(0,-1938,0) rot=(0,0,1;0rad)
  _ExternalGeoVersion = 0
  sketch-geometry (4):
    g0: LineSegment StartX=0 StartY=100 StartZ=0 EndX=600 EndY=100 EndZ=0
    g1: LineSegment StartX=600 StartY=100 StartZ=0 EndX=600 EndY=0 EndZ=0
    g2: LineSegment StartX=600 StartY=0 StartZ=0 EndX=0 EndY=0 EndZ=0
    g3: LineSegment StartX=0 StartY=0 StartZ=0 EndX=0 EndY=100 EndZ=0
  constraints (11):
    c: Coincident(g0,g1)
    c: Coincident(g1,g2)
    c: Coincident(g2,g3)
    c: Coincident(g3,g0)
    c: Horizontal(g0)
    c: Horizontal(g2)
    c: Vertical(g1)
    c: Vertical(g3)
    c: Coincident(g2,g-1)
    c: DistanceX(g0,g0) = 600  'SizeX'
    c: DistanceY(g3,g3) = 100  'SizeY'
FEATURE [PartDesign::Pad] Pad008  label="Profile Angle 1"
  Direction = (0,0,1)
  Length = 100
  Length2 = 10
  Profile = -> Sketch013
  SideType = 0
  Suppressed = false
  Type = 0
  Type2 = 0
FEATURE [PartDesign::Thickness] Angle
  Base = -> Pad008 [Face2,Face4,Face6]
  BaseFeature = -> Pad008
  Intersection = false
  Join = 0
  Mode = 0
  Reversed = true
  SupportTransform = false
  Suppressed = false
  Value = 1
FEATURE [PartDesign::Body] Body009  label="Body, Construction001"
  AllowCompound = false
  Group = -> [Sketch013,Pad008,Angle]
  Origin = -> Origin011
  Tip = -> Angle
COMPONENT P18 — recipe-attached ("Part, Construction002", modeled in this document).
Construction recipe (the document's own serialized feature program — sketch geometry with constraints, then the solid features built on it; lengths are millimeters unless a unit is written):

FEATURE [Sketcher::SketchObject] Sketch014  label="Pattern, Construction002"
  ArcFitTolerance = 0
  AttachmentOffset = pos=(0,-2238,0) rot=(0,0,1;0rad)
  AttachmentSupport = -> [XY_Plane013]
  ExternalTypes = [0]
  FullyConstrained = true
  MakeInternals = false
  MapMode = 5
  Placement = pos=(0,-2238,0) rot=(0,0,1;0rad)
  _ExternalGeoVersion = 0
  sketch-geometry (4):
    g0: LineSegment StartX=0 StartY=100 StartZ=0 EndX=600 EndY=100 EndZ=0
    g1: LineSegment StartX=600 StartY=100 StartZ=0 EndX=600 EndY=0 EndZ=0
    g2: LineSegment StartX=600 StartY=0 StartZ=0 EndX=0 EndY=0 EndZ=0
    g3: LineSegment StartX=0 StartY=0 StartZ=0 EndX=0 EndY=100 EndZ=0
  constraints (11):
    c: Coincident(g0,g1)
    c: Coincident(g1,g2)
    c: Coincident(g2,g3)
    c: Coincident(g3,g0)
    c: Horizontal(g0)
    c: Horizontal(g2)
    c: Vertical(g1)
    c: Vertical(g3)
    c: Coincident(g2,g-1)
    c: DistanceX(g0,g0) = 600  'SizeX'
    c: DistanceY(g3,g3) = 100  'SizeY'
FEATURE [PartDesign::Pad] Pad009  label="Profile Angle 2"
  Direction = (0,0,1)
  Length = 100
  Length2 = 10
  Profile = -> Sketch014
  SideType = 0
  Suppressed = false
  Type = 0
  Type2 = 0
FEATURE [PartDesign::Thickness] Angle001
  Base = -> Pad009 [Face2,Face4,Face3,Face6]
  BaseFeature = -> Pad009
  Intersection = false
  Join = 0
  Mode = 0
  Reversed = true
  SupportTransform = false
  Suppressed = false
  Value = 1
FEATURE [PartDesign::Body] Body010  label="Body, Construction002"
  AllowCompound = false
  Group = -> [Sketch014,Pad009,Angle001]
  Origin = -> Origin013
  Tip = -> Angle001
COMPONENT P19 — recipe-attached ("Part, Construction003", modeled in this document).
Construction recipe (the document's own serialized feature program — sketch geometry with constraints, then the solid features built on it; lengths are millimeters unless a unit is written):

FEATURE [Sketcher::SketchObject] Sketch015  label="Pattern, Construction003"
  ArcFitTolerance = 0
  AttachmentOffset = pos=(0,-2538,0) rot=(0,0,1;0rad)
  AttachmentSupport = -> [XY_Plane015]
  ExternalTypes = [0]
  FullyConstrained = true
  MakeInternals = false
  MapMode = 5
  Placement = pos=(0,-2538,0) rot=(0,0,1;0rad)
  _ExternalGeoVersion = 0
  sketch-geometry (4):
    g0: LineSegment StartX=0 StartY=100 StartZ=0 EndX=600 EndY=100 EndZ=0
    g1: LineSegment StartX=600 StartY=100 StartZ=0 EndX=600 EndY=0 EndZ=0
    g2: LineSegment StartX=600 StartY=0 StartZ=0 EndX=0 EndY=0 EndZ=0
    g3: LineSegment StartX=0 StartY=0 StartZ=0 EndX=0 EndY=100 EndZ=0
  constraints (11):
    c: Coincident(g0,g1)
    c: Coincident(g1,g2)
    c: Coincident(g2,g3)
    c: Coincident(g3,g0)
    c: Horizontal(g0)
    c: Horizontal(g2)
    c: Vertical(g1)
    c: Vertical(g3)
    c: Coincident(g2,g-1)
    c: DistanceX(g0,g0) = 600  'SizeX'
    c: DistanceY(g3,g3) = 100  'SizeY'
FEATURE [PartDesign::Pad] Pad010  label="Profile Angle 45 Cut"
  Direction = (0,0,1)
  Length = 100
  Length2 = 10
  Profile = -> Sketch015
  SideType = 0
  Suppressed = false
  Type = 0
  Type2 = 0
FEATURE [PartDesign::Thickness] Angle002
  Base = -> Pad010 [Face2,Face4,Face3,Face6]
  BaseFeature = -> Pad010
  Intersection = false
  Join = 0
  Mode = 0
  Reversed = true
  SupportTransform = false
  Suppressed = false
  Value = 1
FEATURE [PartDesign::Chamfer] Angle45Cut
  Angle = 45
  Base = -> Angle002 [Edge11,Edge13]
  BaseFeature = -> Angle002
  ChamferType = 0
  FlipDirection = false
  Size = 98.99
  Size2 = 1
  SupportTransform = false
  Suppressed = false
  UseAllEdges = false
FEATURE [PartDesign::Body] Body011  label="Body, Construction003"
  AllowCompound = false
  Group = -> [Sketch015,Pad010,Angle002,Angle45Cut]
  Origin = -> Origin015
  Tip = -> Angle45Cut
COMPONENT P20 — recipe-attached ("Part, Frame", modeled in this document).
Construction recipe (the document's own serialized feature program — sketch geometry with constraints, then the solid features built on it; lengths are millimeters unless a unit is written):

FEATURE [Sketcher::SketchObject] Sketch016  label="Pattern, Frame"
  ArcFitTolerance = 0
  AttachmentOffset = pos=(800,0,1618) rot=(0,0,1;0rad)
  AttachmentSupport = -> [XZ_Plane017]
  ExternalTypes = [0]
  FullyConstrained = true
  MakeInternals = false
  MapMode = 5
  Placement = pos=(800,-1618,3.593e-13) rot=(1,0,0;1.5708rad)
  _ExternalGeoVersion = 0
  sketch-geometry (4):
    g0: LineSegment StartX=0 StartY=40 StartZ=0 EndX=600 EndY=40 EndZ=0
    g1: LineSegment StartX=600 StartY=40 StartZ=0 EndX=600 EndY=0 EndZ=0
    g2: LineSegment StartX=600 StartY=0 StartZ=0 EndX=0 EndY=0 EndZ=0
    g3: LineSegment StartX=0 StartY=0 StartZ=0 EndX=0 EndY=40 EndZ=0
  constraints (11):
    c: Coincident(g0,g1)
    c: Coincident(g1,g2)
    c: Coincident(g2,g3)
    c: Coincident(g3,g0)
    c: Horizontal(g0)
    c: Horizontal(g2)
    c: Vertical(g1)
    c: Vertical(g3)
    c: Coincident(g2,g-1)
    c: DistanceX(g0,g0) = 600  'SizeX'
    c: DistanceY(g3,g3) = 40  'SizeY'
FEATURE [PartDesign::Pad] Pad011  label="Frame"
  Direction = (0,-1,2e-16)
  Length = 20
  Length2 = 10
  Placement = pos=(0,0,0) rot=(1,0,0;1.5708rad)
  Profile = -> Sketch016
  SideType = 0
  Suppressed = false
  Type = 0
  Type2 = 0
FEATURE [PartDesign::Chamfer] Frame45Cut
  Angle = 45
  Base = -> Pad011 [Edge1,Edge2]
  BaseFeature = -> Pad011
  ChamferType = 0
  FlipDirection = false
  Placement = pos=(0,0,0) rot=(1,0,0;1.5708rad)
  Size = 39.99
  Size2 = 1
  SupportTransform = false
  Suppressed = false
  UseAllEdges = false
FEATURE [PartDesign::Body] Body012  label="Body, Frame"
  AllowCompound = false
  Group = -> [Sketch016,Pad011,Frame45Cut]
  Origin = -> Origin017
  Tip = -> Frame45Cut
COMPONENT P21 — recipe-attached ("Part, Frame001", modeled in this document).
Construction recipe (the document's own serialized feature program — sketch geometry with constraints, then the solid features built on it; lengths are millimeters unless a unit is written):

FEATURE [Sketcher::SketchObject] Sketch017  label="Pattern, Frame001"
  ArcFitTolerance = 0
  AttachmentOffset = pos=(800,-1938,0) rot=(0,0,1;0rad)
  AttachmentSupport = -> [XY_Plane019]
  ExternalTypes = [0]
  FullyConstrained = true
  MakeInternals = false
  MapMode = 5
  Placement = pos=(800,-1938,0) rot=(0,0,1;0rad)
  _ExternalGeoVersion = 0
  sketch-geometry (4):
    g0: LineSegment StartX=0 StartY=100 StartZ=0 EndX=600 EndY=100 EndZ=0
    g1: LineSegment StartX=600 StartY=100 StartZ=0 EndX=600 EndY=0 EndZ=0
    g2: LineSegment StartX=600 StartY=0 StartZ=0 EndX=0 EndY=0 EndZ=0
    g3: LineSegment StartX=0 StartY=0 StartZ=0 EndX=0 EndY=100 EndZ=0
  constraints (11):
    c: Coincident(g0,g1)
    c: Coincident(g1,g2)
    c: Coincident(g2,g3)
    c: Coincident(g3,g0)
    c: Horizontal(g0)
    c: Horizontal(g2)
    c: Vertical(g1)
    c: Vertical(g3)
    c: Coincident(g2,g-1)
    c: DistanceX(g0,g0) = 600  'SizeX'
    c: DistanceY(g3,g3) = 100  'SizeY'
FEATURE [PartDesign::Pad] Pad012  label="Frame Table Foot"
  Direction = (0,0,1)
  Length = 100
  Length2 = 10
  Profile = -> Sketch017
  SideType = 0
  Suppressed = false
  Type = 0
  Type2 = 0
FEATURE [PartDesign::Chamfer] Frame45Cut001
  Angle = 45
  Base = -> Pad012 [Edge12,Edge7]
  BaseFeature = -> Pad012
  ChamferType = 0
  FlipDirection = false
  Size = 99.99
  Size2 = 1
  SupportTransform = false
  Suppressed = false
  UseAllEdges = false
FEATURE [Sketcher::SketchObject] routerPattern
  ArcFitTolerance = 0
  ExternalTypes = [0]
  FullyConstrained = true
  MakeInternals = false
  Placement = pos=(1300.01,-1888,100) rot=(1,0,0;1.5708rad)
  _ExternalGeoVersion = 0
  sketch-geometry (4):
    g0: ArcOfCircle CenterX=49.9999 CenterY=-49.9999 CenterZ=0 NormalX=0 NormalY=0 NormalZ=1 AngleXU=0 Radius=49.9999 StartAngle=1.5708 EndAngle=3.14159
    g1: ArcOfCircle CenterX=-49.9999 CenterY=49.9999 CenterZ=0 NormalX=0 NormalY=0 NormalZ=1 AngleXU=0 Radius=49.9999 StartAngle=4.71239 EndAngle=6.28319
    g2: ArcOfCircle CenterX=49.9999 CenterY=49.9999 CenterZ=0 NormalX=0 NormalY=0 NormalZ=1 AngleXU=0 Radius=49.9999 StartAngle=3.14159 EndAngle=4.71239
    g3: ArcOfCircle CenterX=-49.9999 CenterY=-49.9999 CenterZ=0 NormalX=0 NormalY=0 NormalZ=1 AngleXU=0 Radius=49.9999 StartAngle=6.28318 EndAngle=7.85398
  constraints (16):
    c: Equal(g3,g1)
    c: Equal(g1,g2)
    c: Equal(g2,g0)
    c: Vertical(g0,g2)
    c: Horizontal(g3,g0)
    c: Vertical(g1,g3)
    c: Horizontal(g1,g2)
    c: Coincident(g1,g2)
    c: Coincident(g0,g2)
    c: Coincident(g3,g0)
    c: Coincident(g3,g1)
    c: PointOnObject(g1,g-1)
    c: PointOnObject(g1,g-2)
    c: DistanceY(g0,g-1) = 50
    c: Vertical(g0,g0)
    c: Horizontal(g1,g1)
FEATURE [PartDesign::Pocket] router  label="RoundOver2 "
  BaseFeature = -> Frame45Cut001
  Direction = (0,1,-2e-16)
  Length = 5
  Length2 = 5
  Profile = -> routerPattern
  SideType = 2
  Suppressed = false
  Type = 1
  Type2 = 0
FEATURE [Sketcher::SketchObject] routerPattern001
  ArcFitTolerance = 0
  ExternalTypes = [0]
  FullyConstrained = true
  MakeInternals = false
  Placement = pos=(899.99,-1888,100) rot=(1,0,0;1.5708rad)
  _ExternalGeoVersion = 0
  sketch-geometry (4):
    g0: ArcOfCircle CenterX=50 CenterY=-50 CenterZ=0 NormalX=0 NormalY=0 NormalZ=1 AngleXU=0 Radius=50 StartAngle=1.5708 EndAngle=3.14159
    g1: ArcOfCircle CenterX=-50 CenterY=50 CenterZ=0 NormalX=0 NormalY=0 NormalZ=1 AngleXU=0 Radius=50 StartAngle=4.71239 EndAngle=6.28319
    g2: ArcOfCircle CenterX=50 CenterY=50 CenterZ=0 NormalX=0 NormalY=0 NormalZ=1 AngleXU=0 Radius=50 StartAngle=3.14159 EndAngle=4.71239
    g3: ArcOfCircle CenterX=-50 CenterY=-50 CenterZ=0 NormalX=0 NormalY=0 NormalZ=1 AngleXU=0 Radius=50 StartAngle=6.28318 EndAngle=7.85398
  constraints (16):
    c: Equal(g3,g1)
    c: Equal(g1,g2)
    c: Equal(g2,g0)
    c: Vertical(g0,g2)
    c: Horizontal(g3,g0)
    c: Vertical(g1,g3)
    c: Horizontal(g1,g2)
    c: Coincident(g1,g2)
    c: Coincident(g0,g2)
    c: Coincident(g3,g0)
    c: Coincident(g3,g1)
    c: PointOnObject(g1,g-1)
    c: PointOnObject(g1,g-2)
    c: DistanceY(g0,g-1) = 50
    c: Vertical(g0,g0)
    c: Horizontal(g1,g1)
FEATURE [PartDesign::Pocket] router001  label="RoundOver2 001"
  BaseFeature = -> router
  Direction = (0,1,-2e-16)
  Length = 5
  Length2 = 5
  Profile = -> routerPattern001
  SideType = 2
  Suppressed = false
  Type = 1
  Type2 = 0
FEATURE [Sketcher::SketchObject] Sketch018
  ArcFitTolerance = 0
  ExternalTypes = [0]
  FullyConstrained = true
  MakeInternals = false
  MapMode = 5
  Placement = pos=(1200.01,-1888,100) rot=(0,0,1;0rad)
  _ExternalGeoVersion = 0
  sketch-geometry (1):
    g0: Circle CenterX=0 CenterY=0 CenterZ=0 NormalX=0 NormalY=0 NormalZ=1 AngleXU=0 Radius=5
  constraints (2):
    c: Coincident(g0,g-1)
    c: Diameter(g0) = 10  'Hole00Diameter'
FEATURE [PartDesign::Hole] Hole
  BaseFeature = -> router001
  BaseProfileType = 6
  CustomThreadClearance = 0
  Depth = 25
  DepthType = 0
  Diameter = 10
  DrillForDepth = true
  DrillPoint = 1
  DrillPointAngle = 118
  HoleCutCountersinkAngle = 90
  HoleCutCustomValues = false
  HoleCutDepth = 25
  HoleCutDiameter = 10
  HoleCutType = 0
  ModelThread = false
  Profile = -> Sketch018
  Suppressed = false
  Tapered = false
  TaperedAngle = 90
  ThreadClass = 0
  ThreadDepth = 25
  ThreadDepthType = 0
  ThreadDiameter = 10
  ThreadDirection = 0
  ThreadFit = 0
  ThreadSize = 0
  ThreadType = 0
  Threaded = false
  UseCustomThreadClearance = false
FEATURE [Sketcher::SketchObject] Sketch019
  ArcFitTolerance = 0
  ExternalTypes = [0]
  FullyConstrained = true
  MakeInternals = false
  MapMode = 5
  Placement = pos=(1168.01,-1888,100) rot=(0,0,1;0rad)
  _ExternalGeoVersion = 0
  sketch-geometry (1):
    g0: Circle CenterX=0 CenterY=0 CenterZ=0 NormalX=0 NormalY=0 NormalZ=1 AngleXU=0 Radius=5
  constraints (2):
    c: Coincident(g0,g-1)
    c: Diameter(g0) = 10  'Hole00Diameter'
FEATURE [PartDesign::Hole] Hole001
  BaseFeature = -> Hole
  BaseProfileType = 6
  CustomThreadClearance = 0
  Depth = 25
  DepthType = 0
  Diameter = 10
  DrillForDepth = true
  DrillPoint = 1
  DrillPointAngle = 118
  HoleCutCountersinkAngle = 90
  HoleCutCustomValues = false
  HoleCutDepth = 25
  HoleCutDiameter = 10
  HoleCutType = 0
  ModelThread = false
  Profile = -> Sketch019
  Suppressed = false
  Tapered = false
  TaperedAngle = 90
  ThreadClass = 0
  ThreadDepth = 25
  ThreadDepthType = 0
  ThreadDiameter = 10
  ThreadDirection = 0
  ThreadFit = 0
  ThreadSize = 0
  ThreadType = 0
  Threaded = false
  UseCustomThreadClearance = false
FEATURE [Sketcher::SketchObject] Sketch020
  ArcFitTolerance = 0
  ExternalTypes = [0]
  FullyConstrained = true
  MakeInternals = false
  MapMode = 5
  Placement = pos=(999.99,-1888,100) rot=(0,0,1;0rad)
  _ExternalGeoVersion = 0
  sketch-geometry (1):
    g0: Circle CenterX=0 CenterY=0 CenterZ=0 NormalX=0 NormalY=0 NormalZ=1 AngleXU=0 Radius=5
  constraints (2):
    c: Coincident(g0,g-1)
    c: Diameter(g0) = 10  'Hole00Diameter'
FEATURE [PartDesign::Hole] Hole002
  BaseFeature = -> Hole001
  BaseProfileType = 6
  CustomThreadClearance = 0
  Depth = 25
  DepthType = 0
  Diameter = 10
  DrillForDepth = true
  DrillPoint = 1
  DrillPointAngle = 118
  HoleCutCountersinkAngle = 90
  HoleCutCustomValues = false
  HoleCutDepth = 25
  HoleCutDiameter = 10
  HoleCutType = 0
  ModelThread = false
  Profile = -> Sketch020
  Suppressed = false
  Tapered = false
  TaperedAngle = 90
  ThreadClass = 0
  ThreadDepth = 25
  ThreadDepthType = 0
  ThreadDiameter = 10
  ThreadDirection = 0
  ThreadFit = 0
  ThreadSize = 0
  ThreadType = 0
  Threaded = false
  UseCustomThreadClearance = false
FEATURE [Sketcher::SketchObject] Sketch021
  ArcFitTolerance = 0
  ExternalTypes = [0]
  FullyConstrained = true
  MakeInternals = false
  MapMode = 5
  Placement = pos=(1031.99,-1888,100) rot=(0,0,1;0rad)
  _ExternalGeoVersion = 0
  sketch-geometry (1):
    g0: Circle CenterX=0 CenterY=0 CenterZ=0 NormalX=0 NormalY=0 NormalZ=1 AngleXU=0 Radius=5
  constraints (2):
    c: Coincident(g0,g-1)
    c: Diameter(g0) = 10  'Hole00Diameter'
FEATURE [PartDesign::Hole] Hole003
  BaseFeature = -> Hole002
  BaseProfileType = 6
  CustomThreadClearance = 0
  Depth = 25
  DepthType = 0
  Diameter = 10
  DrillForDepth = true
  DrillPoint = 1
  DrillPointAngle = 118
  HoleCutCountersinkAngle = 90
  HoleCutCustomValues = false
  HoleCutDepth = 25
  HoleCutDiameter = 10
  HoleCutType = 0
  ModelThread = false
  Profile = -> Sketch021
  Suppressed = false
  Tapered = false
  TaperedAngle = 90
  ThreadClass = 0
  ThreadDepth = 25
  ThreadDepthType = 0
  ThreadDiameter = 10
  ThreadDirection = 0
  ThreadFit = 0
  ThreadSize = 0
  ThreadType = 0
  Threaded = false
  UseCustomThreadClearance = false
FEATURE [PartDesign::Body] Body013  label="Body, Frame001"
  AllowCompound = false
  Group = -> [Sketch017,Pad012,Frame45Cut001,routerPattern,router,routerPattern001,router001,Sketch018,Hole,Sketch019,Hole001,Sketch020,Hole002,Sketch021,Hole003]
  Origin = -> Origin019
  Tip = -> Hole003
COMPONENT P22 — recipe-attached ("Part, Holes", modeled in this document).
Construction recipe (the document's own serialized feature program — sketch geometry with constraints, then the solid features built on it; lengths are millimeters unless a unit is written):

FEATURE [Sketcher::SketchObject] Sketch022  label="Pattern, panel with dowels"
  ArcFitTolerance = 0
  AttachmentOffset = pos=(-918,0,2250) rot=(0,0,1;0rad)
  AttachmentSupport = -> [XZ_Plane021]
  ExternalTypes = [0]
  FullyConstrained = true
  MakeInternals = false
  MapMode = 5
  Placement = pos=(-918,-2250,4.996e-13) rot=(1,0,0;1.5708rad)
  _ExternalGeoVersion = 0
  sketch-geometry (4):
    g0: LineSegment StartX=0 StartY=300 StartZ=0 EndX=600 EndY=300 EndZ=0
    g1: LineSegment StartX=600 StartY=300 StartZ=0 EndX=600 EndY=0 EndZ=0
    g2: LineSegment StartX=600 StartY=0 StartZ=0 EndX=0 EndY=0 EndZ=0
    g3: LineSegment StartX=0 StartY=0 StartZ=0 EndX=0 EndY=300 EndZ=0
  constraints (11):
    c: Coincident(g0,g1)
    c: Coincident(g1,g2)
    c: Coincident(g2,g3)
    c: Coincident(g3,g0)
    c: Horizontal(g0)
    c: Horizontal(g2)
    c: Vertical(g1)
    c: Vertical(g3)
    c: Coincident(g2,g-1)
    c: DistanceX(g0,g0) = 600  'SizeX'
    c: DistanceY(g3,g3) = 300  'SizeY'
FEATURE [PartDesign::Pad] Pad013  label="panel with holes"
  Direction = (0,-1,2e-16)
  Length = 18
  Length2 = 10
  Placement = pos=(0,0,0) rot=(1,0,0;1.5708rad)
  Profile = -> Sketch022
  SideType = 0
  Suppressed = false
  Type = 0
  Type2 = 0
FEATURE [Sketcher::SketchObject] Sketch023
  ArcFitTolerance = 0
  ExternalTypes = [0]
  FullyConstrained = true
  MakeInternals = false
  MapMode = 5
  Placement = pos=(-368,-2259,300) rot=(0,0,1;0rad)
  _ExternalGeoVersion = 0
  sketch-geometry (1):
    g0: Circle CenterX=0 CenterY=0 CenterZ=0 NormalX=0 NormalY=0 NormalZ=1 AngleXU=0 Radius=4
  constraints (2):
    c: Coincident(g0,g-1)
    c: Diameter(g0) = 8  'Hole00Diameter'
FEATURE [PartDesign::Hole] Hole004
  BaseFeature = -> Pad013
  BaseProfileType = 6
  CustomThreadClearance = 0
  Depth = 35
  DepthType = 0
  Diameter = 8
  DrillForDepth = true
  DrillPoint = 1
  DrillPointAngle = 118
  HoleCutCountersinkAngle = 90
  HoleCutCustomValues = false
  HoleCutDepth = 35
  HoleCutDiameter = 8
  HoleCutType = 0
  ModelThread = false
  Placement = pos=(0,0,0) rot=(1,0,0;1.5708rad)
  Profile = -> Sketch023
  Suppressed = false
  Tapered = false
  TaperedAngle = 90
  ThreadClass = 0
  ThreadDepth = 35
  ThreadDepthType = 0
  ThreadDiameter = 8
  ThreadDirection = 0
  ThreadFit = 0
  ThreadSize = 0
  ThreadType = 0
  Threaded = false
  UseCustomThreadClearance = false
FEATURE [Sketcher::SketchObject] Sketch024
  ArcFitTolerance = 0
  ExternalTypes = [0]
  FullyConstrained = true
  MakeInternals = false
  MapMode = 5
  Placement = pos=(-400,-2259,300) rot=(0,0,1;0rad)
  _ExternalGeoVersion = 0
  sketch-geometry (1):
    g0: Circle CenterX=0 CenterY=0 CenterZ=0 NormalX=0 NormalY=0 NormalZ=1 AngleXU=0 Radius=4
  constraints (2):
    c: Coincident(g0,g-1)
    c: Diameter(g0) = 8  'Hole00Diameter'
FEATURE [PartDesign::Hole] Hole005
  BaseFeature = -> Hole004
  BaseProfileType = 6
  CustomThreadClearance = 0
  Depth = 35
  DepthType = 0
  Diameter = 8
  DrillForDepth = true
  DrillPoint = 1
  DrillPointAngle = 118
  HoleCutCountersinkAngle = 90
  HoleCutCustomValues = false
  HoleCutDepth = 35
  HoleCutDiameter = 8
  HoleCutType = 0
  ModelThread = false
  Placement = pos=(0,0,0) rot=(1,0,0;1.5708rad)
  Profile = -> Sketch024
  Suppressed = false
  Tapered = false
  TaperedAngle = 90
  ThreadClass = 0
  ThreadDepth = 35
  ThreadDepthType = 0
  ThreadDiameter = 8
  ThreadDirection = 0
  ThreadFit = 0
  ThreadSize = 0
  ThreadType = 0
  Threaded = false
  UseCustomThreadClearance = false
FEATURE [Sketcher::SketchObject] Sketch025
  ArcFitTolerance = 0
  ExternalTypes = [0]
  FullyConstrained = true
  MakeInternals = false
  MapMode = 5
  Placement = pos=(-868,-2259,300) rot=(0,0,1;0rad)
  _ExternalGeoVersion = 0
  sketch-geometry (1):
    g0: Circle CenterX=0 CenterY=0 CenterZ=0 NormalX=0 NormalY=0 NormalZ=1 AngleXU=0 Radius=4
  constraints (2):
    c: Coincident(g0,g-1)
    c: Diameter(g0) = 8  'Hole00Diameter'
FEATURE [PartDesign::Hole] Hole006
  BaseFeature = -> Hole005
  BaseProfileType = 6
  CustomThreadClearance = 0
  Depth = 35
  DepthType = 0
  Diameter = 8
  DrillForDepth = true
  DrillPoint = 1
  DrillPointAngle = 118
  HoleCutCountersinkAngle = 90
  HoleCutCustomValues = false
  HoleCutDepth = 35
  HoleCutDiameter = 8
  HoleCutType = 0
  ModelThread = false
  Placement = pos=(0,0,0) rot=(1,0,0;1.5708rad)
  Profile = -> Sketch025
  Suppressed = false
  Tapered = false
  TaperedAngle = 90
  ThreadClass = 0
  ThreadDepth = 35
  ThreadDepthType = 0
  ThreadDiameter = 8
  ThreadDirection = 0
  ThreadFit = 0
  ThreadSize = 0
  ThreadType = 0
  Threaded = false
  UseCustomThreadClearance = false
FEATURE [Sketcher::SketchObject] Sketch026
  ArcFitTolerance = 0
  ExternalTypes = [0]
  FullyConstrained = true
  MakeInternals = false
  MapMode = 5
  Placement = pos=(-836,-2259,300) rot=(0,0,1;0rad)
  _ExternalGeoVersion = 0
  sketch-geometry (1):
    g0: Circle CenterX=0 CenterY=0 CenterZ=0 NormalX=0 NormalY=0 NormalZ=1 AngleXU=0 Radius=4
  constraints (2):
    c: Coincident(g0,g-1)
    c: Diameter(g0) = 8  'Hole00Diameter'
FEATURE [PartDesign::Hole] Hole007
  BaseFeature = -> Hole006
  BaseProfileType = 6
  CustomThreadClearance = 0
  Depth = 35
  DepthType = 0
  Diameter = 8
  DrillForDepth = true
  DrillPoint = 1
  DrillPointAngle = 118
  HoleCutCountersinkAngle = 90
  HoleCutCustomValues = false
  HoleCutDepth = 35
  HoleCutDiameter = 8
  HoleCutType = 0
  ModelThread = false
  Placement = pos=(0,0,0) rot=(1,0,0;1.5708rad)
  Profile = -> Sketch026
  Suppressed = false
  Tapered = false
  TaperedAngle = 90
  ThreadClass = 0
  ThreadDepth = 35
  ThreadDepthType = 0
  ThreadDiameter = 8
  ThreadDirection = 0
  ThreadFit = 0
  ThreadSize = 0
  ThreadType = 0
  Threaded = false
  UseCustomThreadClearance = false
FEATURE [Sketcher::SketchObject] Sketch027
  ArcFitTolerance = 0
  ExternalTypes = [0]
  FullyConstrained = true
  MakeInternals = false
  MapMode = 5
  Placement = pos=(-327,-2268,250) rot=(1,0,0;1.5708rad)
  _ExternalGeoVersion = 0
  sketch-geometry (2):
    g0: Circle CenterX=0 CenterY=0 CenterZ=0 NormalX=0 NormalY=0 NormalZ=1 AngleXU=0 Radius=1.5
    g1: Circle [constr] CenterX=0 CenterY=0 CenterZ=0 NormalX=0 NormalY=0 NormalZ=1 AngleXU=0 Radius=5
  constraints (4):
    c: Coincident(g0,g-1)
    c: Diameter(g0) = 3  'Hole00Diameter'
    c: Coincident(g1,g-1)
    c: Diameter(g1) = 10  'Countersink00Diameter'
FEATURE [PartDesign::Hole] Countersink
  BaseFeature = -> Hole007
  BaseProfileType = 6
  CustomThreadClearance = 0
  Depth = 40
  DepthType = 0
  Diameter = 3
  DrillForDepth = true
  DrillPoint = 1
  DrillPointAngle = 118
  HoleCutCountersinkAngle = 90
  HoleCutCustomValues = false
  HoleCutDepth = 5
  HoleCutDiameter = 10
  HoleCutType = 2
  ModelThread = false
  Placement = pos=(0,0,0) rot=(1,0,0;1.5708rad)
  Profile = -> Sketch027
  Suppressed = false
  Tapered = false
  TaperedAngle = 90
  ThreadClass = 0
  ThreadDepth = 40
  ThreadDepthType = 0
  ThreadDiameter = 3
  ThreadDirection = 0
  ThreadFit = 0
  ThreadSize = 0
  ThreadType = 0
  Threaded = false
  UseCustomThreadClearance = false
FEATURE [Sketcher::SketchObject] Sketch028
  ArcFitTolerance = 0
  ExternalTypes = [0]
  FullyConstrained = true
  MakeInternals = false
  MapMode = 5
  Placement = pos=(-327,-2268,50) rot=(1,0,0;1.5708rad)
  _ExternalGeoVersion = 0
  sketch-geometry (2):
    g0: Circle CenterX=0 CenterY=0 CenterZ=0 NormalX=0 NormalY=0 NormalZ=1 AngleXU=0 Radius=1.5
    g1: Circle [constr] CenterX=0 CenterY=0 CenterZ=0 NormalX=0 NormalY=0 NormalZ=1 AngleXU=0 Radius=5
  constraints (4):
    c: Coincident(g0,g-1)
    c: Diameter(g0) = 3  'Hole00Diameter'
    c: Coincident(g1,g-1)
    c: Diameter(g1) = 10  'Countersink00Diameter'
FEATURE [PartDesign::Hole] Countersink001
  BaseFeature = -> Countersink
  BaseProfileType = 6
  CustomThreadClearance = 0
  Depth = 40
  DepthType = 0
  Diameter = 3
  DrillForDepth = true
  DrillPoint = 1
  DrillPointAngle = 118
  HoleCutCountersinkAngle = 90
  HoleCutCustomValues = false
  HoleCutDepth = 5
  HoleCutDiameter = 10
  HoleCutType = 2
  ModelThread = false
  Placement = pos=(0,0,0) rot=(1,0,0;1.5708rad)
  Profile = -> Sketch028
  Suppressed = false
  Tapered = false
  TaperedAngle = 90
  ThreadClass = 0
  ThreadDepth = 40
  ThreadDepthType = 0
  ThreadDiameter = 3
  ThreadDirection = 0
  ThreadFit = 0
  ThreadSize = 0
  ThreadType = 0
  Threaded = false
  UseCustomThreadClearance = false
FEATURE [Sketcher::SketchObject] Sketch029
  ArcFitTolerance = 0
  ExternalTypes = [0]
  FullyConstrained = true
  MakeInternals = false
  MapMode = 5
  Placement = pos=(-858,-2274,250) rot=(0.677661,0.519988,0.519988;1.95044rad)
  _ExternalGeoVersion = 0
  sketch-geometry (2):
    g0: Circle CenterX=0 CenterY=0 CenterZ=0 NormalX=0 NormalY=0 NormalZ=1 AngleXU=0 Radius=1.5
    g1: Circle [constr] CenterX=0 CenterY=0 CenterZ=0 NormalX=0 NormalY=0 NormalZ=1 AngleXU=0 Radius=4.75
  constraints (4):
    c: Coincident(g0,g-1)
    c: Diameter(g0) = 3  'Tip0hole00Diameter'
    c: Coincident(g1,g-1)
    c: Diameter(g1) = 9.5  'Pocket0hole00Diameter'
FEATURE [PartDesign::Hole] PocketHole
  BaseFeature = -> Countersink001
  BaseProfileType = 6
  CustomThreadClearance = 0
  Depth = 90
  DepthType = 0
  Diameter = 3
  DrillForDepth = false
  DrillPoint = 0
  DrillPointAngle = 118
  HoleCutCountersinkAngle = 90
  HoleCutCustomValues = false
  HoleCutDepth = 45
  HoleCutDiameter = 9.5
  HoleCutType = 1
  ModelThread = false
  Placement = pos=(0,0,0) rot=(1,0,0;1.5708rad)
  Profile = -> Sketch029
  Suppressed = false
  Tapered = false
  TaperedAngle = 90
  ThreadClass = 0
  ThreadDepth = 90
  ThreadDepthType = 0
  ThreadDiameter = 3
  ThreadDirection = 0
  ThreadFit = 0
  ThreadSize = 0
  ThreadType = 0
  Threaded = false
  UseCustomThreadClearance = false
FEATURE [Sketcher::SketchObject] Sketch030
  ArcFitTolerance = 0
  ExternalTypes = [0]
  FullyConstrained = true
  MakeInternals = false
  MapMode = 5
  Placement = pos=(-858,-2274,218) rot=(0.677661,0.519988,0.519988;1.95044rad)
  _ExternalGeoVersion = 0
  sketch-geometry (2):
    g0: Circle CenterX=0 CenterY=0 CenterZ=0 NormalX=0 NormalY=0 NormalZ=1 AngleXU=0 Radius=1.5
    g1: Circle [constr] CenterX=0 CenterY=0 CenterZ=0 NormalX=0 NormalY=0 NormalZ=1 AngleXU=0 Radius=4.75
  constraints (4):
    c: Coincident(g0,g-1)
    c: Diameter(g0) = 3  'Tip0hole00Diameter'
    c: Coincident(g1,g-1)
    c: Diameter(g1) = 9.5  'Pocket0hole00Diameter'
FEATURE [PartDesign::Hole] PocketHole001
  BaseFeature = -> PocketHole
  BaseProfileType = 6
  CustomThreadClearance = 0
  Depth = 90
  DepthType = 0
  Diameter = 3
  DrillForDepth = false
  DrillPoint = 0
  DrillPointAngle = 118
  HoleCutCountersinkAngle = 90
  HoleCutCustomValues = false
  HoleCutDepth = 45
  HoleCutDiameter = 9.5
  HoleCutType = 1
  ModelThread = false
  Placement = pos=(0,0,0) rot=(1,0,0;1.5708rad)
  Profile = -> Sketch030
  Suppressed = false
  Tapered = false
  TaperedAngle = 90
  ThreadClass = 0
  ThreadDepth = 90
  ThreadDepthType = 0
  ThreadDiameter = 3
  ThreadDirection = 0
  ThreadFit = 0
  ThreadSize = 0
  ThreadType = 0
  Threaded = false
  UseCustomThreadClearance = false
FEATURE [Sketcher::SketchObject] Sketch031
  ArcFitTolerance = 0
  ExternalTypes = [0]
  FullyConstrained = true
  MakeInternals = false
  MapMode = 5
  Placement = pos=(-858,-2274,50) rot=(0.677661,0.519988,0.519988;1.95044rad)
  _ExternalGeoVersion = 0
  sketch-geometry (2):
    g0: Circle CenterX=0 CenterY=0 CenterZ=0 NormalX=0 NormalY=0 NormalZ=1 AngleXU=0 Radius=1.5
    g1: Circle [constr] CenterX=0 CenterY=0 CenterZ=0 NormalX=0 NormalY=0 NormalZ=1 AngleXU=0 Radius=4.75
  constraints (4):
    c: Coincident(g0,g-1)
    c: Diameter(g0) = 3  'Tip0hole00Diameter'
    c: Coincident(g1,g-1)
    c: Diameter(g1) = 9.5  'Pocket0hole00Diameter'
FEATURE [PartDesign::Hole] PocketHole002
  BaseFeature = -> PocketHole001
  BaseProfileType = 6
  CustomThreadClearance = 0
  Depth = 90
  DepthType = 0
  Diameter = 3
  DrillForDepth = false
  DrillPoint = 0
  DrillPointAngle = 118
  HoleCutCountersinkAngle = 90
  HoleCutCustomValues = false
  HoleCutDepth = 45
  HoleCutDiameter = 9.5
  HoleCutType = 1
  ModelThread = false
  Placement = pos=(0,0,0) rot=(1,0,0;1.5708rad)
  Profile = -> Sketch031
  Suppressed = false
  Tapered = false
  TaperedAngle = 90
  ThreadClass = 0
  ThreadDepth = 90
  ThreadDepthType = 0
  ThreadDiameter = 3
  ThreadDirection = 0
  ThreadFit = 0
  ThreadSize = 0
  ThreadType = 0
  Threaded = false
  UseCustomThreadClearance = false
FEATURE [Sketcher::SketchObject] Sketch032
  ArcFitTolerance = 0
  ExternalTypes = [0]
  FullyConstrained = true
  MakeInternals = false
  MapMode = 5
  Placement = pos=(-858,-2274,82) rot=(0.677661,0.519988,0.519988;1.95044rad)
  _ExternalGeoVersion = 0
  sketch-geometry (2):
    g0: Circle CenterX=0 CenterY=0 CenterZ=0 NormalX=0 NormalY=0 NormalZ=1 AngleXU=0 Radius=1.5
    g1: Circle [constr] CenterX=0 CenterY=0 CenterZ=0 NormalX=0 NormalY=0 NormalZ=1 AngleXU=0 Radius=4.75
  constraints (4):
    c: Coincident(g0,g-1)
    c: Diameter(g0) = 3  'Tip0hole00Diameter'
    c: Coincident(g1,g-1)
    c: Diameter(g1) = 9.5  'Pocket0hole00Diameter'
FEATURE [PartDesign::Hole] PocketHole003
  BaseFeature = -> PocketHole002
  BaseProfileType = 6
  CustomThreadClearance = 0
  Depth = 90
  DepthType = 0
  Diameter = 3
  DrillForDepth = false
  DrillPoint = 0
  DrillPointAngle = 118
  HoleCutCountersinkAngle = 90
  HoleCutCustomValues = false
  HoleCutDepth = 45
  HoleCutDiameter = 9.5
  HoleCutType = 1
  ModelThread = false
  Placement = pos=(0,0,0) rot=(1,0,0;1.5708rad)
  Profile = -> Sketch032
  Suppressed = false
  Tapered = false
  TaperedAngle = 90
  ThreadClass = 0
  ThreadDepth = 90
  ThreadDepthType = 0
  ThreadDiameter = 3
  ThreadDirection = 0
  ThreadFit = 0
  ThreadSize = 0
  ThreadType = 0
  Threaded = false
  UseCustomThreadClearance = false
FEATURE [PartDesign::Body] Body014  label="Body, Holes"
  AllowCompound = false
  Group = -> [Sketch022,Pad013,Sketch023,Hole004,Sketch024,Hole005,Sketch025,Hole006,Sketch026,Hole007,Sketch027,Countersink,Sketch028,Countersink001,Sketch029,PocketHole,Sketch030,PocketHole001,Sketch031,PocketHole002,Sketch032,PocketHole003]
  Origin = -> Origin021
  Tip = -> PocketHole003
COMPONENT P23 — recipe-attached ("Part, panel2pad", modeled in this document).
Construction recipe (the document's own serialized feature program — sketch geometry with constraints, then the solid features built on it; lengths are millimeters unless a unit is written):

FEATURE [Sketcher::SketchObject] Sketch033  label="Pattern, panel2pad"
  ArcFitTolerance = 0
  AttachmentOffset = pos=(2502,0,1582) rot=(0,0,1;0rad)
  AttachmentSupport = -> [XZ_Plane023]
  ExternalTypes = [0]
  FullyConstrained = true
  MakeInternals = false
  MapMode = 5
  Placement = pos=(2502,-1582,3.513e-13) rot=(1,0,0;1.5708rad)
  _ExternalGeoVersion = 0
  sketch-geometry (4):
    g0: LineSegment StartX=0 StartY=300 StartZ=0 EndX=600 EndY=300 EndZ=0
    g1: LineSegment StartX=600 StartY=300 StartZ=0 EndX=600 EndY=0 EndZ=0
    g2: LineSegment StartX=600 StartY=0 StartZ=0 EndX=0 EndY=0 EndZ=0
    g3: LineSegment StartX=0 StartY=0 StartZ=0 EndX=0 EndY=300 EndZ=0
  constraints (11):
    c: Coincident(g0,g1)
    c: Coincident(g1,g2)
    c: Coincident(g2,g3)
    c: Coincident(g3,g0)
    c: Horizontal(g0)
    c: Horizontal(g2)
    c: Vertical(g1)
    c: Vertical(g3)
    c: Coincident(g2,g-1)
    c: DistanceX(g0,g0) = 600  'SizeX'
    c: DistanceY(g3,g3) = 300  'SizeY'
FEATURE [PartDesign::Pad] Pad014  label="panel Mortise and Tenon"
  Direction = (0,-1,2e-16)
  Length = 18
  Length2 = 10
  Placement = pos=(0,0,0) rot=(1,0,0;1.5708rad)
  Profile = -> Sketch033
  SideType = 0
  Suppressed = false
  Type = 0
  Type2 = 0
FEATURE [Sketcher::SketchObject] Sketch034  label="Joint Pattern"
  ArcFitTolerance = 0
  AttachmentSupport = -> [Pad014]
  ExternalTypes = [0]
  FullyConstrained = true
  MakeInternals = false
  MapMode = 5
  Placement = pos=(0,1.32e-13,300) rot=(0,0,1;3.14159rad)
  _ExternalGeoVersion = 0
  sketch-geometry (4):
    g0: ArcOfCircle CenterX=0 CenterY=-7 CenterZ=0 NormalX=0 NormalY=0 NormalZ=1 AngleXU=0 Radius=3 StartAngle=3.14159 EndAngle=6.28319
    g1: ArcOfCircle CenterX=0 CenterY=7 CenterZ=0 NormalX=0 NormalY=0 NormalZ=1 AngleXU=0 Radius=3 StartAngle=1e-16 EndAngle=3.14159
    g2: LineSegment StartX=3 StartY=-7 StartZ=0 EndX=3 EndY=7 EndZ=0
    g3: LineSegment StartX=-3 StartY=7 StartZ=0 EndX=-3 EndY=-7 EndZ=0
  constraints (9):
    c: Tangent(g0,g2) = -1.5708
    c: Tangent(g2,g1) = -1.5708
    c: Tangent(g1,g3) = -1.5708
    c: Tangent(g3,g0) = -1.5708
    c: Equal(g0,g1)
    c: PointOnObject(g1,g-2)
    c: Symmetric(g1,g0,g-1)
    c: DistanceY(g3,g3) = 14
    c: Radius(g1) = 3
FEATURE [Part::Part2DObjectPython] Clone2D001  label="Pattern from Joint Pattern 001"  # Draft 2D object (typed FeaturePython)
  ForceCompound = false
  Fuse = false
  Objects = -> [Sketch034]
  Placement = pos=(2552,-1591,300) rot=(0,0,1;1.5708rad)
  Scale = (1,1,1)
FEATURE [PartDesign::Pad] Tenon  label="Tenon "
  BaseFeature = -> Pad014
  Direction = (0,0,1)
  Length = 30
  Length2 = 10
  Placement = pos=(0,0,0) rot=(1,0,0;1.5708rad)
  Profile = -> Clone2D001
  SideType = 2
  Suppressed = false
  Type = 0
  Type2 = 0
FEATURE [Part::Part2DObjectPython] Clone2D002  label="Pattern from Joint Pattern 002"  # Draft 2D object (typed FeaturePython)
  ForceCompound = false
  Fuse = false
  Objects = -> [Sketch034]
  Placement = pos=(2584,-1591,300) rot=(0,0,1;1.5708rad)
  Scale = (1,1,1)
FEATURE [PartDesign::Pad] Tenon001  label="Tenon 001"
  BaseFeature = -> Tenon
  Direction = (0,0,1)
  Length = 30
  Length2 = 10
  Placement = pos=(0,0,0) rot=(1,0,0;1.5708rad)
  Profile = -> Clone2D002
  SideType = 2
  Suppressed = false
  Type = 0
  Type2 = 0
FEATURE [Part::Part2DObjectPython] Clone2D003  label="Pattern from Joint Pattern 003"  # Draft 2D object (typed FeaturePython)
  ForceCompound = false
  Fuse = false
  Objects = -> [Sketch034]
  Placement = pos=(3020,-1591,300) rot=(0,0,1;1.5708rad)
  Scale = (1,1,1)
FEATURE [PartDesign::Pad] Tenon002  label="Tenon 002"
  BaseFeature = -> Tenon001
  Direction = (0,0,1)
  Length = 30
  Length2 = 10
  Placement = pos=(0,0,0) rot=(1,0,0;1.5708rad)
  Profile = -> Clone2D003
  SideType = 2
  Suppressed = false
  Type = 0
  Type2 = 0
FEATURE [Part::Part2DObjectPython] Clone2D004  label="Pattern from Joint Pattern 004"  # Draft 2D object (typed FeaturePython)
  ForceCompound = false
  Fuse = false
  Objects = -> [Sketch034]
  Placement = pos=(2988,-1591,300) rot=(0,0,1;1.5708rad)
  Scale = (1,1,1)
FEATURE [PartDesign::Pad] Tenon003  label="Tenon 003"
  BaseFeature = -> Tenon002
  Direction = (0,0,1)
  Length = 30
  Length2 = 10
  Placement = pos=(0,0,0) rot=(1,0,0;1.5708rad)
  Profile = -> Clone2D004
  SideType = 2
  Suppressed = false
  Type = 0
  Type2 = 0
FEATURE [Part::Part2DObjectPython] Clone2D005  label="Pattern from Joint Pattern 005"  # Draft 2D object (typed FeaturePython)
  ForceCompound = false
  Fuse = false
  Objects = -> [Sketch034]
  Placement = pos=(3093,-1600,250) rot=(0,0.707107,0.707107;3.14159rad)
  Scale = (1,1,1)
FEATURE [PartDesign::Pocket] Mortise  label="Mortise "
  BaseFeature = -> Tenon003
  Direction = (-1e-16,-1,2e-16)
  Length = 30
  Length2 = 5
  Placement = pos=(0,0,0) rot=(1,0,0;1.5708rad)
  Profile = -> Clone2D005
  SideType = 2
  Suppressed = false
  Type = 0
  Type2 = 0
FEATURE [Part::Part2DObjectPython] Clone2D006  label="Pattern from Joint Pattern 006"  # Draft 2D object (typed FeaturePython)
  ForceCompound = false
  Fuse = false
  Objects = -> [Sketch034]
  Placement = pos=(3093,-1600,218) rot=(0,0.707107,0.707107;3.14159rad)
  Scale = (1,1,1)
FEATURE [PartDesign::Pocket] Mortise001  label="Mortise 001"
  BaseFeature = -> Mortise
  Direction = (-1e-16,-1,2e-16)
  Length = 30
  Length2 = 5
  Placement = pos=(0,0,0) rot=(1,0,0;1.5708rad)
  Profile = -> Clone2D006
  SideType = 2
  Suppressed = false
  Type = 0
  Type2 = 0
FEATURE [Part::Part2DObjectPython] Clone2D007  label="Pattern from Joint Pattern 007"  # Draft 2D object (typed FeaturePython)
  ForceCompound = false
  Fuse = false
  Objects = -> [Sketch034]
  Placement = pos=(3093,-1600,82) rot=(0,0.707107,0.707107;3.14159rad)
  Scale = (1,1,1)
FEATURE [PartDesign::Pocket] Mortise002  label="Mortise 002"
  BaseFeature = -> Mortise001
  Direction = (-1e-16,-1,2e-16)
  Length = 30
  Length2 = 5
  Placement = pos=(0,0,0) rot=(1,0,0;1.5708rad)
  Profile = -> Clone2D007
  SideType = 2
  Suppressed = false
  Type = 0
  Type2 = 0
FEATURE [Part::Part2DObjectPython] Clone2D008  label="Pattern from Joint Pattern 008"  # Draft 2D object (typed FeaturePython)
  ForceCompound = false
  Fuse = false
  Objects = -> [Sketch034]
  Placement = pos=(3093,-1600,50) rot=(0,0.707107,0.707107;3.14159rad)
  Scale = (1,1,1)
FEATURE [PartDesign::Pocket] Mortise003  label="Mortise 003"
  BaseFeature = -> Mortise002
  Direction = (-1e-16,-1,2e-16)
  Length = 30
  Length2 = 5
  Placement = pos=(0,0,0) rot=(1,0,0;1.5708rad)
  Profile = -> Clone2D008
  SideType = 2
  Suppressed = false
  Type = 0
  Type2 = 0
FEATURE [PartDesign::Body] Body015  label="Body, panel2pad"
  AllowCompound = false
  Group = -> [Sketch033,Pad014,Sketch034,Clone2D001,Tenon,Clone2D002,Tenon001,Clone2D003,Tenon002,Clone2D004,Tenon003,Clone2D005,Mortise,Clone2D006,Mortise001,Clone2D007,Mortise002,Clone2D008,Mortise003]
  Origin = -> Origin023
  Tip = -> Mortise003
COMPONENT P24 — geometry summary ("Part009"; no construction recipe available for this part):
  bounding box: 790.4 x 630.7 x 100.0 mm
  tessellated surface: 12 triangles
  volume: 13698095 mm^3 (27% of its bounding box)
  symmetry: 2-fold rotationally symmetric about the z axis; mirror-symmetric across its z mid-plane
COMPONENT P25 — recipe-attached ("Part010", modeled in this document).
Construction recipe (the document's own serialized feature program — sketch geometry with constraints, then the solid features built on it; lengths are millimeters unless a unit is written):

FEATURE [Sketcher::SketchObject] Sketch039
  ArcFitTolerance = 1e-06
  AttachmentSupport = -> [Origin056]
  ExternalTypes = [0]
  FullyConstrained = false
  MakeInternals = false
  MapMode = 5
  _ExternalGeoVersion = 0
  sketch-geometry (3):
    g0: ArcOfCircle CenterX=283.785 CenterY=-4018.61 CenterZ=0 NormalX=0 NormalY=0 NormalZ=1 AngleXU=0 Radius=206.877 StartAngle=0.831397 EndAngle=3.08456
    g1: ArcOfCircle CenterX=668.902 CenterY=-3779.66 CenterZ=0 NormalX=0 NormalY=0 NormalZ=1 AngleXU=0 Radius=260.358 StartAngle=3.47859 EndAngle=5.83442
    g2: ArcOfCircle CenterX=1150.68 CenterY=-4079.25 CenterZ=0 NormalX=0 NormalY=0 NormalZ=1 AngleXU=0 Radius=309.735 StartAngle=0.702222 EndAngle=2.49491
  constraints (2):
    c: Coincident(g1,g0)
    c: Coincident(g2,g1)
FEATURE [PartDesign::Body] Body017  label="Body"
  AllowCompound = true
  Group = -> [Sketch039]
  Origin = -> Origin056
COMPONENT P26 — recipe-attached ("Part, panel2pad002", modeled in this document).
Construction recipe (the document's own serialized feature program — sketch geometry with constraints, then the solid features built on it; lengths are millimeters unless a unit is written):

FEATURE [Sketcher::SketchObject] Sketch040  label="Pattern, panel2pad002"
  ArcFitTolerance = 1e-06
  AttachmentOffset = pos=(-3879.18,0,1827.13) rot=(0,1,0;0rad)
  AttachmentSupport = -> [YZ_Plane030]
  ExternalTypes = [0]
  FullyConstrained = true
  MakeInternals = false
  MapMode = 5
  Placement = pos=(1827.13,-3879.18,0) rot=(0.57735,0.57735,0.57735;2.0944rad)
  _ExternalGeoVersion = 1
  sketch-geometry (5):
    g0: LineSegment StartX=500 StartY=0 StartZ=0 EndX=0 EndY=0 EndZ=0
    g1: LineSegment StartX=0 StartY=0 StartZ=0 EndX=0 EndY=600 EndZ=0
    g2: LineSegment StartX=0 StartY=600 StartZ=0 EndX=250 EndY=600 EndZ=0
    g3: LineSegment StartX=500 StartY=0 StartZ=0 EndX=500 EndY=350 EndZ=0
    g4: ArcOfCircle CenterX=250 CenterY=350 CenterZ=0 NormalX=0 NormalY=0 NormalZ=1 AngleXU=0 Radius=250 StartAngle=0 EndAngle=1.5708
  constraints (13):
    c: Coincident(g0,g1)
    c: Horizontal(g0)
    c: Vertical(g1)
    c: Coincident(g0,g-1)
    c: DistanceY(g1,g1) = 600  'SizeY'
    c: DistanceX(g0,g0) = 500  'SizeX'
    c: Coincident(g2,g1)
    c: Horizontal(g2)
    c: Coincident(g3,g0)
    c: Vertical(g3)
    c: Tangent(g4,g2) = 1.5708
    c: Tangent(g4,g3) = -1.5708
    c: DistanceX(g-1,g4) = 250
FEATURE [PartDesign::Pad] Pad016  label="along curve - left"
  Direction = (1,0,0)
  Length = 18
  Length2 = 10
  Placement = pos=(0,0,0) rot=(1,1,1;2.0944rad)
  Profile = -> Sketch040
  Refine = true
  SideType = 0
  Suppressed = false
  Type = 0
  Type2 = 0
FEATURE [PartDesign::Body] Body018  label="Body, panel2pad002"
  AllowCompound = true
  Group = -> [Sketch040,Pad016]
  Origin = -> Origin060
  Tip = -> Pad016
COMPONENT P27 — recipe-attached ("Part, vertices2sketch ", modeled in this document).
Construction recipe (the document's own serialized feature program — sketch geometry with constraints, then the solid features built on it; lengths are millimeters unless a unit is written):

FEATURE [Sketcher::SketchObject] Sketch041  label="Pattern, vertices2sketch "
  ArcFitTolerance = 1e-06
  ExternalTypes = [0]
  FullyConstrained = false
  MakeInternals = false
  Placement = pos=(0,0,1.3283e-12) rot=(0,0,-1;3.14159rad)
  _ExternalGeoVersion = 1
  sketch-geometry (4):
    g0: LineSegment StartX=-1845.13 StartY=3397.18 StartZ=0 EndX=-1845.13 EndY=3379.18 EndZ=0
    g1: LineSegment StartX=-1845.13 StartY=3379.18 StartZ=0 EndX=-2245.13 EndY=3379.18 EndZ=0
    g2: LineSegment StartX=-2245.13 StartY=3379.18 StartZ=0 EndX=-2245.13 EndY=3397.18 EndZ=0
    g3: LineSegment StartX=-2245.13 StartY=3397.18 StartZ=0 EndX=-1845.13 EndY=3397.18 EndZ=0
  constraints (8):
    c: Coincident(g1,g2)
    c: Coincident(g2,g3)
    c: Coincident(g0,g1)
    c: Coincident(g0,g3)
    c: Vertical(g0)
    c: Horizontal(g1)
    c: Vertical(g2)
    c: Horizontal(g3)
FEATURE [PartDesign::SubShapeBinder] Binder  label="curve"
  BindCopyOnChange = 0
  BindMode = 0
  ClaimChildren = false
  Context = -> Part012 [Body019.Binder.]
  Fuse = false
  MakeFace = true
  OffsetFill = false
  OffsetIntersection = false
  OffsetJoinType = 0
  OffsetOpenResult = false
  PartialLoad = false
  Refine = true
  Relative = true
  Support = -> [Part011[Body018.Pad016.Edge15,Body018.Pad016.Edge13,Body018.Pad016.Edge10]]
  _Version = 2
FEATURE [PartDesign::AdditivePipe] curve2panel
  AuxiliaryCurvilinear = true
  AuxiliarySpineTangent = false
  Binormal = (0,0,0)
  Mode = 0
  Placement = pos=(0,0,1.3283e-12) rot=(0,0,-1;3.14159rad)
  Profile = -> Sketch041
  Refine = true
  Spine = -> Binder [Edge1,Edge2,Edge3]
  SpineTangent = false
  Suppressed = false
  Transformation = 0
  Transition = 0
  Woodworking_Height = 18
  Woodworking_Length = 992.699
  Woodworking_Width = 400
FEATURE [PartDesign::Body] Body019  label="Body, vertices2sketch "
  AllowCompound = true
  Group = -> [Sketch041,Binder,curve2panel]
  Origin = -> Origin064
  Tip = -> curve2panel
PROVENANCE & LICENSES
A FreeCAD (.FCStd) document from a public repository crawl; recipes are the document's own serialized feature recipes (and, for linked parts, companion documents' recipes).
License: mit.
